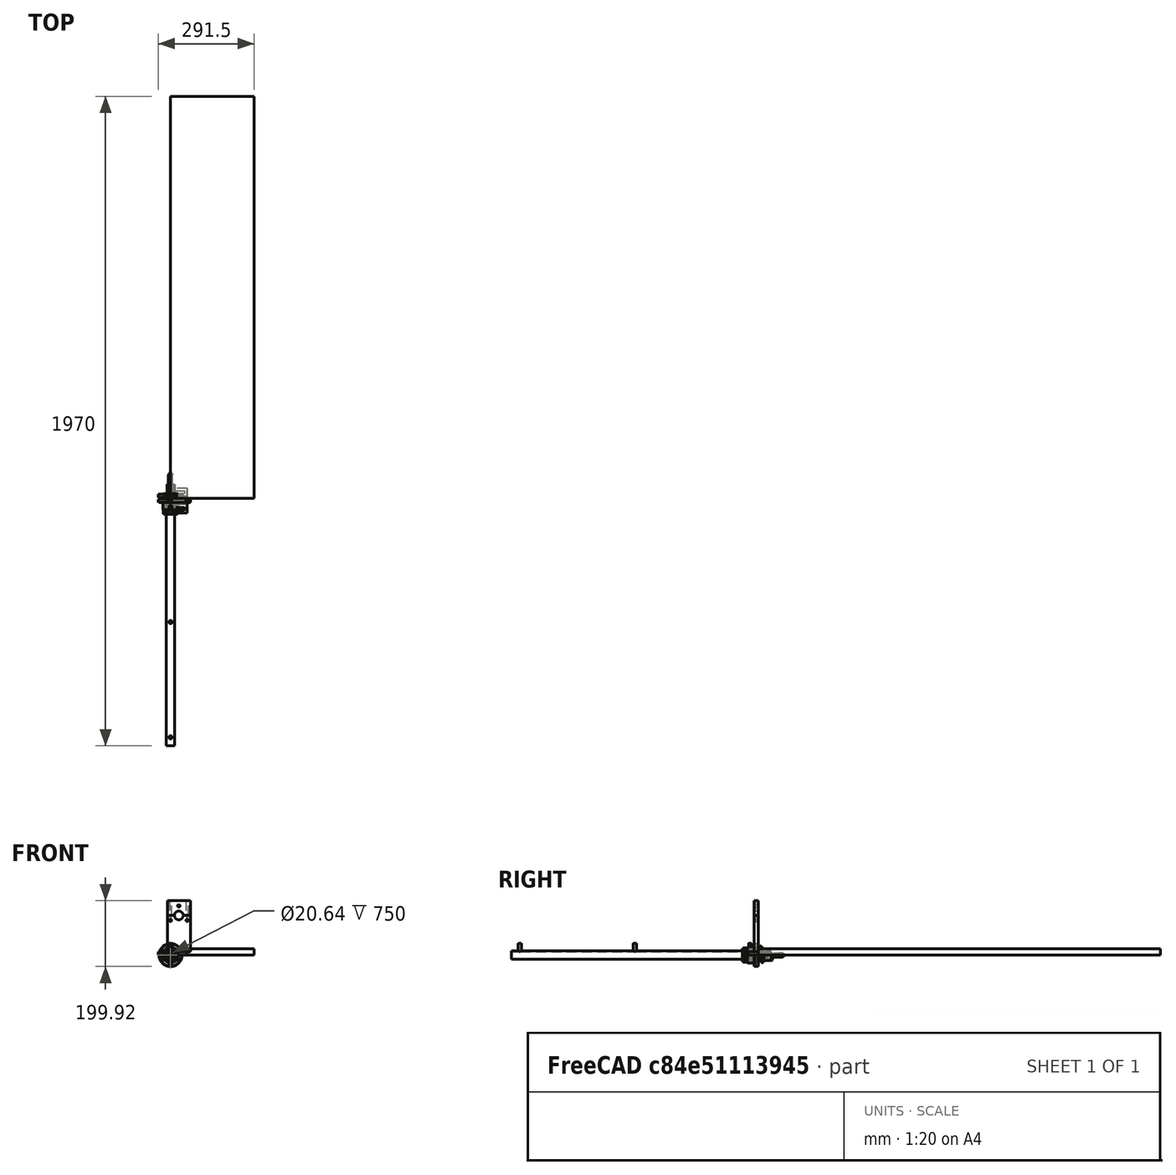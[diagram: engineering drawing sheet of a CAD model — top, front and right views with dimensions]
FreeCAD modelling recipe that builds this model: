
FCSTD DOCUMENT  (FreeCAD 0.19R24291 (Git))
Label: CEAS2a
License: All rights reserved
LicenseURL: http://en.wikipedia.org/wiki/All_rights_reserved
objects: Part::Feature×69, Part::Cut×64, Sketcher::SketchObject×60, PartDesign::Pad×60, PartDesign::Body×59, Part::Compound2×15, App::Part×14, TechDraw::DrawViewPart×8, Part::Chamfer×6, Part::MultiFuse×5, TechDraw::DrawViewDimension×4, TechDraw::DrawViewBalloon×4, TechDraw::DrawViewAnnotation×4, Part::Fillet×2, TechDraw::DrawSVGTemplate×1, TechDraw::DrawPage×1, Part::Sphere×1
note: 386 computed .brp shape members not serialized (recipe doc carries the construction recipe); baked Part::Feature solids carry a one-line shape summary decoded from their .brp

FEATURE [Sketcher::SketchObject] Sketch
  FullyConstrained = true
  MapMode = 5
  Support = -> [XY_Plane001]
  sketch-geometry (4):
    g0: LineSegment StartX=0 StartY=1220 StartZ=0 EndX=254 EndY=1220 EndZ=0
    g1: LineSegment StartX=254 StartY=1220 StartZ=0 EndX=254 EndY=0 EndZ=0
    g2: LineSegment StartX=254 StartY=0 StartZ=0 EndX=0 EndY=0 EndZ=0
    g3: LineSegment StartX=0 StartY=0 StartZ=0 EndX=0 EndY=1220 EndZ=0
  constraints (11):
    c: Coincident(g0,g1)
    c: Coincident(g1,g2)
    c: Coincident(g2,g3)
    c: Coincident(g3,g0)
    c: Horizontal(g0)
    c: Horizontal(g2)
    c: Vertical(g1)
    c: Vertical(g3)
    c: DistanceY(g3,g3) = 1220
    c: Coincident(g2,g-1)
    c: DistanceX(g2,g2) = 254
FEATURE [PartDesign::Pad] Pad
  AllowMultiFace = false
  Direction = (1,1,1)
  Length = 19.05
  Length2 = 100
  Profile = -> Sketch
  Type = 0
FEATURE [PartDesign::Body] Body  label="BasePlate001"
  Group = -> [Sketch,Pad]
  Origin = -> Origin001
  Tip = -> Pad
FEATURE [App::Part] Part  label="BasePlate"
  Group = -> [Body]
  Origin = -> Origin
FEATURE [Sketcher::SketchObject] Sketch001
  FullyConstrained = true
  MapMode = 5
  Placement = pos=(0,0,0) rot=(1,0,0;1.5708rad)
  Support = -> [XZ_Plane003]
  sketch-geometry (6):
    g0: LineSegment StartX=0 StartY=0 StartZ=0 EndX=0 EndY=110 EndZ=0
    g1: LineSegment StartX=0 StartY=110 StartZ=0 EndX=21.675 EndY=110 EndZ=0
    g2: ArcOfCircle CenterX=35 CenterY=110 CenterZ=0 NormalX=0 NormalY=0 NormalZ=1 AngleXU=0 Radius=13.325 StartAngle=3.14159 EndAngle=6.28319
    g3: LineSegment StartX=48.325 StartY=110 StartZ=0 EndX=70 EndY=110 EndZ=0
    g4: LineSegment StartX=70 StartY=110 StartZ=0 EndX=70 EndY=0 EndZ=0
    g5: LineSegment StartX=70 StartY=0 StartZ=0 EndX=0 EndY=0 EndZ=0
  constraints (18):
    c: DistanceX(g5,g5) = 70
    c: Coincident(g5,g0)
    c: Coincident(g1,g2)
    c: Coincident(g1,g0)
    c: Coincident(g2,g3)
    c: Coincident(g3,g4)
    c: Coincident(g5,g4)
    c: Diameter(g2) = 26.65
    c: Parallel(g0,g4)
    c: DistanceY(g4,g4) = 110
    c: Equal(g0,g4)
    c: Equal(g3,g1)
    c: Perpendicular(g5,g0)
    c: Perpendicular(g4,g3)
    c: Vertical(g0)
    c: Perpendicular(g0,g1)
    c: Coincident(g0,g-1)
    c: DistanceX(g1,g2) = 26.65
FEATURE [Sketcher::SketchObject] Sketch002
  FullyConstrained = true
  MapMode = 5
  Placement = pos=(0,0,0) rot=(1,0,0;1.5708rad)
  Support = -> [XZ_Plane004]
  sketch-geometry (6):
    g0: LineSegment StartX=-20 StartY=110 StartZ=0 EndX=-20 EndY=155 EndZ=0
    g1: LineSegment StartX=-20 StartY=155 StartZ=0 EndX=50 EndY=155 EndZ=0
    g2: LineSegment StartX=50 StartY=155 StartZ=0 EndX=50 EndY=110 EndZ=0
    g3: LineSegment StartX=50 StartY=110 StartZ=0 EndX=28.325 EndY=110 EndZ=0
    g4: LineSegment StartX=-20 StartY=110 StartZ=0 EndX=1.675 EndY=110 EndZ=0
    g5: ArcOfCircle CenterX=15 CenterY=110 CenterZ=0 NormalX=0 NormalY=0 NormalZ=1 AngleXU=0 Radius=13.325 StartAngle=2.48459e-06 EndAngle=3.14159
  constraints (19):
    c: Diameter(g5) = 26.65
    c: DistanceX(g1,g1) = 70
    c: Coincident(g0,g1)
    c: Coincident(g1,g2)
    c: Coincident(g2,g3)
    c: Coincident(g5,g3)
    c: Coincident(g5,g4)
    c: Coincident(g0,g4)
    c: DistanceY(g2,g2) = 45
    c: Equal(g2,g0)
    c: Horizontal(g4)
    c: Equal(g4,g3)
    c: Vertical(g0)
    c: Horizontal(g1)
    c: Perpendicular(g2,g1)
    c: Perpendicular(g2,g3)
    c: DistanceY(g-1,g0) = 110
    c: DistanceX(g-1,g2) = 50
    c: DistanceX(g4,g3) = 26.65
FEATURE [PartDesign::Pad] Pad001
  AllowMultiFace = false
  Direction = (1,1,1)
  Length = 12.7
  Length2 = 100
  Placement = pos=(0,0,0) rot=(1,0,0;1.5708rad)
  Profile = -> Sketch001
  Type = 0
FEATURE [PartDesign::Body] Body001  label="BraceLower"
  Group = -> [Sketch001,Pad001]
  Origin = -> Origin003
  Placement = pos=(-10,0,10) rot=(0,0,1;0rad)
  Tip = -> Pad001
FEATURE [PartDesign::Pad] Pad002
  AllowMultiFace = false
  Direction = (1,1,1)
  Length = 12.7
  Length2 = 100
  Placement = pos=(0,0,0) rot=(1,0,0;1.5708rad)
  Profile = -> Sketch002
  Type = 0
FEATURE [PartDesign::Body] Body002  label="Brace1Upper"
  Group = -> [Sketch002,Pad002]
  Origin = -> Origin004
  Placement = pos=(10,0,10) rot=(0,0,1;0rad)
  Tip = -> Pad002
FEATURE [Part::Feature] Solid  label="19227-E0W"
  Placement = pos=(25,-6.35,5.1905) rot=(1,0,0;1.5708rad)
  shape: bbox 50 x 75 x 10 mm, 234 faces (baked)
FEATURE [Part::Feature] Solid002  label="19225-E0W"
  Placement = pos=(0,0,5) rot=(1,0,0;1.5708rad)
  shape: bbox 75 x 24.99 x 10 mm, 221 faces (baked)
FEATURE [Part::Feature] Solid003
  shape: bbox 25 x 75 x 25 mm, 25 faces (baked)
FEATURE [Part::Feature] Solid004
  shape: bbox 15.88 x 5.969 x 15.88 mm, 19 faces (baked)
FEATURE [Part::Feature] Solid005
  shape: bbox 14.48 x 14.48 x 16.13 mm, 310 faces (baked)
FEATURE [Part::Feature] Solid006
  shape: bbox 2.997 x 2.997 x 3.556 mm, 8 faces (baked)
FEATURE [Part::Feature] Solid007
  shape: bbox 3.52 x 3.049 x 7.519 mm, 25 faces (baked)
FEATURE [Part::Feature] Solid008
  shape: bbox 3.482 x 3.482 x 3.175 mm, 21 faces (baked)
FEATURE [Part::Compound2] Compound  label="23133-E0W"
  Links = -> [Solid003,Solid004,Solid005,Solid006,Solid007,Solid008]
  Placement = pos=(-1.27,-4.75,41.95) rot=(1,0,0;1.5708rad)
FEATURE [Part::Feature] Solid009
  shape: bbox 12.67 x 75.01 x 12.67 mm, 32 faces (baked)
FEATURE [Part::Feature] Solid010
  shape: bbox 4.001 x 12 x 4.001 mm, 40 faces (baked)
FEATURE [Part::Compound2] Compound001  label="0332-E0W"
  Links = -> [Solid009,Solid010]
  Placement = pos=(0,0,22.896) rot=(1,0,0;1.5708rad)
FEATURE [Part::Feature] Solid011
  shape: bbox 30.48 x 37.34 x 10.16 mm, 236 faces (baked)
FEATURE [Part::Feature] Solid012
  shape: bbox 26.29 x 26.29 x 2.032 mm, 29 faces (baked)
FEATURE [Part::Compound2] Compound002  label="0001-E0W"
  Links = -> [Solid011,Solid012]
  Placement = pos=(0,-5.05,120) rot=(1,0,0;1.5708rad)
FEATURE [App::Part] Part003  label="Lens1"
  Group = -> [Solid002,Solid008,Solid006,Solid003,Solid005,Solid007,Solid004,Compound,Solid009,Solid010,Compound001,Solid012,Solid011,Compound002]
  Origin = -> Origin008
  Placement = pos=(127,100,19.05) rot=(0,0,1;0rad)
FEATURE [Part::Feature] Solid013  label="19225-E0W001"
  Placement = pos=(0,0,5) rot=(1,0,0;1.5708rad)
  shape: bbox 75 x 24.99 x 10 mm, 221 faces (baked)
FEATURE [Part::Feature] Solid014
  shape: bbox 25 x 75 x 25 mm, 25 faces (baked)
FEATURE [Part::Feature] Solid015
  shape: bbox 15.88 x 5.969 x 15.88 mm, 19 faces (baked)
FEATURE [Part::Feature] Solid016
  shape: bbox 14.48 x 14.48 x 16.13 mm, 310 faces (baked)
FEATURE [Part::Feature] Solid017
  shape: bbox 2.997 x 2.997 x 3.556 mm, 8 faces (baked)
FEATURE [Part::Feature] Solid018
  shape: bbox 3.52 x 3.049 x 7.519 mm, 25 faces (baked)
FEATURE [Part::Feature] Solid019
  shape: bbox 3.482 x 3.482 x 3.175 mm, 21 faces (baked)
FEATURE [Part::Compound2] Compound003  label="23133-E0W001"
  Links = -> [Solid014,Solid015,Solid016,Solid017,Solid018,Solid019]
  Placement = pos=(-1.27,-4.75,41.95) rot=(1,0,0;1.5708rad)
FEATURE [Part::Feature] Solid020
  shape: bbox 12.67 x 75.01 x 12.67 mm, 32 faces (baked)
FEATURE [Part::Feature] Solid021
  shape: bbox 4.001 x 12 x 4.001 mm, 40 faces (baked)
FEATURE [Part::Compound2] Compound004  label="0332-E0W001"
  Links = -> [Solid020,Solid021]
  Placement = pos=(0,0,22.896) rot=(1,0,0;1.5708rad)
FEATURE [Part::Feature] Solid022
  shape: bbox 30.48 x 37.34 x 10.16 mm, 236 faces (baked)
FEATURE [Part::Feature] Solid023
  shape: bbox 26.29 x 26.29 x 2.032 mm, 29 faces (baked)
FEATURE [Part::Compound2] Compound005  label="0001-E0W001"
  Links = -> [Solid022,Solid023]
  Placement = pos=(0,-5.05,120) rot=(1,0,0;1.5708rad)
FEATURE [App::Part] Part004  label="Lens2"
  Group = -> [Solid013,Solid019,Solid017,Solid014,Solid016,Solid018,Solid015,Compound003,Solid020,Solid021,Compound004,Solid023,Solid022,Compound005]
  Origin = -> Origin009
  Placement = pos=(127,200,19.05) rot=(0,0,1;0rad)
FEATURE [Part::Feature] Solid024
  shape: bbox 26.29 x 26.29 x 2.032 mm, 29 faces (baked)
FEATURE [Part::Feature] Solid025
  shape: bbox 30.48 x 37.34 x 10.16 mm, 236 faces (baked)
FEATURE [Part::Compound2] Compound006  label="0001-E0W002"
  Links = -> [Solid025,Solid024]
  Placement = pos=(0,-5.05,120) rot=(1,0,0;1.5708rad)
FEATURE [Part::Feature] Solid026
  shape: bbox 2.997 x 2.997 x 3.556 mm, 8 faces (baked)
FEATURE [Part::Feature] Solid027
  shape: bbox 14.48 x 14.48 x 16.13 mm, 310 faces (baked)
FEATURE [Part::Feature] Solid028
  shape: bbox 25 x 75 x 25 mm, 25 faces (baked)
FEATURE [Part::Feature] Solid029
  shape: bbox 15.88 x 5.969 x 15.88 mm, 19 faces (baked)
FEATURE [Part::Feature] Solid030
  shape: bbox 3.482 x 3.482 x 3.175 mm, 21 faces (baked)
FEATURE [Part::Feature] Solid031
  shape: bbox 3.52 x 3.049 x 7.519 mm, 25 faces (baked)
FEATURE [Part::Compound2] Compound007  label="23133-E0W002"
  Links = -> [Solid028,Solid029,Solid027,Solid026,Solid031,Solid030]
  Placement = pos=(-1.27,-4.75,41.95) rot=(1,0,0;1.5708rad)
FEATURE [Part::Feature] Solid032  label="19225-E0W002"
  Placement = pos=(0,0,5) rot=(1,0,0;1.5708rad)
  shape: bbox 75 x 24.99 x 10 mm, 221 faces (baked)
FEATURE [Part::Feature] Solid033
  shape: bbox 12.67 x 75.01 x 12.67 mm, 32 faces (baked)
FEATURE [Part::Feature] Solid034
  shape: bbox 4.001 x 12 x 4.001 mm, 40 faces (baked)
FEATURE [Part::Compound2] Compound008  label="0332-E0W002"
  Links = -> [Solid033,Solid034]
  Placement = pos=(0,0,22.896) rot=(1,0,0;1.5708rad)
FEATURE [App::Part] Part005  label="Lens3"
  Group = -> [Solid032,Solid030,Solid026,Solid028,Solid027,Solid031,Solid029,Compound007,Solid033,Solid034,Compound008,Solid024,Solid025,Compound006]
  Origin = -> Origin010
  Placement = pos=(127,1150,19.05) rot=(0,0,1;0rad)
FEATURE [Sketcher::SketchObject] Sketch005
  FullyConstrained = true
  MapMode = 5
  Placement = pos=(0,0,0) rot=(1,0,0;1.5708rad)
  Support = -> [XZ_Plane015]
  sketch-geometry (2):
    g0: Circle CenterX=0 CenterY=0 CenterZ=0 NormalX=0 NormalY=0 NormalZ=1 AngleXU=0 Radius=12.7
    g1: Circle CenterX=0 CenterY=0 CenterZ=0 NormalX=0 NormalY=0 NormalZ=1 AngleXU=0 Radius=10.3187
  constraints (4):
    c: Coincident(g0,g-1)
    c: Coincident(g1,g0)
    c: Diameter(g0) = 25.4
    c: Diameter(g1) = 20.6375
FEATURE [PartDesign::Pad] Pad005
  Direction = (1,1,1)
  Length = 750
  Length2 = 100
  Placement = pos=(0,0,0) rot=(1,0,0;1.5708rad)
  Profile = -> Sketch005
  Type = 0
FEATURE [PartDesign::Body] Body005
  Group = -> [Sketch005,Pad005]
  Origin = -> Origin015
  Tip = -> Pad005
FEATURE [Sketcher::SketchObject] Sketch006
  FullyConstrained = true
  MapMode = 5
  Support = -> [XY_Plane016]
  sketch-geometry (2):
    g0: Circle CenterX=0 CenterY=0 CenterZ=0 NormalX=0 NormalY=0 NormalZ=1 AngleXU=0 Radius=4.7625
    g1: Circle CenterX=0 CenterY=0 CenterZ=0 NormalX=0 NormalY=0 NormalZ=1 AngleXU=0 Radius=3.8695
  constraints (4):
    c: Coincident(g0,g-1)
    c: Coincident(g1,g0)
    c: Diameter(g0) = 9.525
    c: Diameter(g1) = 7.739
FEATURE [PartDesign::Pad] Pad006
  Direction = (1,1,1)
  Length = 25.4
  Length2 = 100
  Profile = -> Sketch006
  Type = 0
FEATURE [PartDesign::Body] Body006
  Group = -> [Sketch006,Pad006]
  Origin = -> Origin016
  Placement = pos=(0,-25.4,9.55) rot=(0,0,1;0rad)
  Tip = -> Pad006
FEATURE [Sketcher::SketchObject] Sketch007
  FullyConstrained = true
  MapMode = 5
  Support = -> [XY_Plane017]
  sketch-geometry (2):
    g0: Circle CenterX=0 CenterY=0 CenterZ=0 NormalX=0 NormalY=0 NormalZ=1 AngleXU=0 Radius=4.7625
    g1: Circle CenterX=0 CenterY=0 CenterZ=0 NormalX=0 NormalY=0 NormalZ=1 AngleXU=0 Radius=3.8695
  constraints (4):
    c: Coincident(g0,g-1)
    c: Coincident(g1,g0)
    c: Diameter(g0) = 9.525
    c: Diameter(g1) = 7.739
FEATURE [PartDesign::Pad] Pad007
  Direction = (1,1,1)
  Length = 25.4
  Length2 = 100
  Profile = -> Sketch007
  Type = 0
FEATURE [PartDesign::Body] Body007
  Group = -> [Sketch007,Pad007]
  Origin = -> Origin017
  Placement = pos=(0,-375,9.55) rot=(0,0,1;0rad)
  Tip = -> Pad007
FEATURE [Sketcher::SketchObject] Sketch008
  FullyConstrained = true
  MapMode = 5
  Support = -> [XY_Plane018]
  sketch-geometry (2):
    g0: Circle CenterX=0 CenterY=0 CenterZ=0 NormalX=0 NormalY=0 NormalZ=1 AngleXU=0 Radius=4.7625
    g1: Circle CenterX=0 CenterY=0 CenterZ=0 NormalX=0 NormalY=0 NormalZ=1 AngleXU=0 Radius=3.8695
  constraints (4):
    c: Coincident(g0,g-1)
    c: Coincident(g1,g0)
    c: Diameter(g0) = 9.525
    c: Diameter(g1) = 7.739
FEATURE [PartDesign::Pad] Pad008
  Direction = (1,1,1)
  Length = 25.4
  Length2 = 100
  Profile = -> Sketch008
  Type = 0
FEATURE [PartDesign::Body] Body008
  Group = -> [Sketch008,Pad008]
  Origin = -> Origin018
  Placement = pos=(0,-724.6,9.55) rot=(0,0,1;0rad)
  Tip = -> Pad008
FEATURE [Sketcher::SketchObject] Sketch009
  FullyConstrained = true
  MapMode = 5
  Support = -> [XY_Plane020]
  sketch-geometry (1):
    g0: Circle CenterX=0 CenterY=0 CenterZ=0 NormalX=0 NormalY=0 NormalZ=1 AngleXU=0 Radius=4.7625
  constraints (2):
    c: Coincident(g0,g-1)
    c: Diameter(g0) = 9.525
FEATURE [PartDesign::Pad] Pad009
  Direction = (1,1,1)
  Length = 25.4
  Length2 = 100
  Profile = -> Sketch009
  Type = 0
FEATURE [PartDesign::Body] Body009
  Group = -> [Sketch009,Pad009]
  Origin = -> Origin019
  Placement = pos=(0,-25.4,0) rot=(0,0,1;0rad)
  Tip = -> Pad009
FEATURE [Sketcher::SketchObject] Sketch010
  FullyConstrained = true
  MapMode = 5
  Support = -> [XY_Plane021]
  sketch-geometry (1):
    g0: Circle CenterX=0 CenterY=0 CenterZ=0 NormalX=0 NormalY=0 NormalZ=1 AngleXU=0 Radius=4.7625
  constraints (2):
    c: Coincident(g0,g-1)
    c: Diameter(g0) = 9.525
FEATURE [PartDesign::Pad] Pad010
  Direction = (1,1,1)
  Length = 25.4
  Length2 = 100
  Profile = -> Sketch010
  Type = 0
FEATURE [PartDesign::Body] Body010
  Group = -> [Sketch010,Pad010]
  Origin = -> Origin020
  Placement = pos=(0,-375,0) rot=(0,0,1;0rad)
  Tip = -> Pad010
FEATURE [Sketcher::SketchObject] Sketch011
  FullyConstrained = true
  MapMode = 5
  Support = -> [XY_Plane022]
  sketch-geometry (1):
    g0: Circle CenterX=0 CenterY=0 CenterZ=0 NormalX=0 NormalY=0 NormalZ=1 AngleXU=0 Radius=4.7625
  constraints (2):
    c: Coincident(g0,g-1)
    c: Diameter(g0) = 9.525
FEATURE [PartDesign::Pad] Pad011
  Direction = (1,1,1)
  Length = 25.4
  Length2 = 100
  Profile = -> Sketch011
  Type = 0
FEATURE [PartDesign::Body] Body011
  Group = -> [Sketch011,Pad011]
  Origin = -> Origin021
  Placement = pos=(0,-724.6,0) rot=(0,0,1;0rad)
  Tip = -> Pad011
FEATURE [Part::Cut] Cut
  Base = -> Body005
  Tool = -> Body009
FEATURE [Part::Cut] Cut001
  Base = -> Cut
  Tool = -> Body010
FEATURE [Part::Cut] Cut002
  Base = -> Cut001
  Tool = -> Body011
FEATURE [Sketcher::SketchObject] Sketch012
  FullyConstrained = true
  MapMode = 5
  Placement = pos=(0,0,0) rot=(1,0,0;1.5708rad)
  Support = -> [XZ_Plane022]
  sketch-geometry (1):
    g0: Circle CenterX=0 CenterY=0 CenterZ=0 NormalX=0 NormalY=0 NormalZ=1 AngleXU=0 Radius=10.3187
  constraints (2):
    c: Coincident(g0,g-1)
    c: Diameter(g0) = 20.6375
FEATURE [PartDesign::Pad] Pad012
  Direction = (1,1,1)
  Length = 750
  Length2 = 100
  Placement = pos=(0,0,0) rot=(1,0,0;1.5708rad)
  Profile = -> Sketch012
  Type = 0
FEATURE [PartDesign::Body] Body012
  Group = -> [Sketch012,Pad012]
  Origin = -> Origin022
  Tip = -> Pad012
FEATURE [Part::Cut] Cut003
  Base = -> Body006
  Tool = -> Body012
FEATURE [Part::Cut] Cut004
  Base = -> Body007
  Tool = -> Body012
FEATURE [Part::Cut] Cut005
  Base = -> Body008
  Tool = -> Body012
FEATURE [Part::MultiFuse] Fusion
  Shapes = -> [Cut002,Cut005,Cut004,Cut003]
FEATURE [App::Part] Part007  label="Cavity"
  Group = -> [Body005,Body006,Body007,Body008,Body009,Body010,Body011,Cut,Cut001,Cut002,Body012,Cut005,Cut004,Cut003,Fusion]
  Origin = -> Origin014
  Placement = pos=(127,310.4,139.05) rot=(0,0,1;3.14159rad)
FEATURE [Sketcher::SketchObject] Sketch013
  FullyConstrained = true
  MapMode = 5
  Placement = pos=(0,0,0) rot=(1,0,0;1.5708rad)
  Support = -> [XZ_Plane024]
  sketch-geometry (2):
    g0: Circle CenterX=0 CenterY=0 CenterZ=0 NormalX=0 NormalY=0 NormalZ=1 AngleXU=0 Radius=34.925
    g1: Circle CenterX=0 CenterY=0 CenterZ=0 NormalX=0 NormalY=0 NormalZ=1 AngleXU=0 Radius=14.2875
  constraints (4):
    c: Coincident(g0,g-1)
    c: Coincident(g1,g0)
    c: Diameter(g1) = 28.575
    c: Diameter(g0) = 69.85
FEATURE [PartDesign::Pad] Pad013
  Direction = (1,1,1)
  Length = 12.7
  Length2 = 100
  Placement = pos=(0,0,0) rot=(1,0,0;1.5708rad)
  Profile = -> Sketch013
  Type = 0
FEATURE [PartDesign::Body] Body013
  Group = -> [Sketch013,Pad013]
  Origin = -> Origin024
  Tip = -> Pad013
FEATURE [Sketcher::SketchObject] Sketch014
  FullyConstrained = true
  MapMode = 5
  Placement = pos=(0,0,0) rot=(1,0,0;1.5708rad)
  Support = -> [XZ_Plane025]
  sketch-geometry (1):
    g0: Circle CenterX=0 CenterY=29.3687 CenterZ=0 NormalX=0 NormalY=0 NormalZ=1 AngleXU=0 Radius=3.57187
  constraints (3):
    c: PointOnObject(g0,g-2)
    c: DistanceY(g-1,g0) = 29.3687
    c: Diameter(g0) = 7.14375
FEATURE [PartDesign::Pad] Pad014
  Direction = (1,1,1)
  Length = 13
  Length2 = 100
  Placement = pos=(0,0,0) rot=(1,0,0;1.5708rad)
  Profile = -> Sketch014
  Type = 0
FEATURE [PartDesign::Body] Body014
  Group = -> [Sketch014,Pad014]
  Origin = -> Origin025
  Tip = -> Pad014
FEATURE [Part::Cut] Cut006
  Base = -> Body013
  Placement = pos=(0,0,0) rot=(0,1,0;1.0472rad)
  Tool = -> Body014
FEATURE [Part::Cut] Cut007
  Base = -> Cut006
  Placement = pos=(0,0,0) rot=(0,1,0;1.0472rad)
  Tool = -> Body014
FEATURE [Part::Cut] Cut008
  Base = -> Cut007
  Placement = pos=(0,0,0) rot=(0,1,0;1.0472rad)
  Tool = -> Body014
FEATURE [Part::Cut] Cut009
  Base = -> Cut008
  Placement = pos=(0,0,0) rot=(0,1,0;1.0472rad)
  Tool = -> Body014
FEATURE [Part::Cut] Cut010
  Base = -> Cut009
  Placement = pos=(0,0,0) rot=(0,1,0;1.0472rad)
  Tool = -> Body014
FEATURE [Part::Cut] Cut011
  Base = -> Cut010
  Tool = -> Body014
FEATURE [Sketcher::SketchObject] Sketch015
  FullyConstrained = true
  MapMode = 5
  Placement = pos=(0,0,0) rot=(1,0,0;1.5708rad)
  Support = -> [XZ_Plane026]
  sketch-geometry (2):
    g0: Circle CenterX=0 CenterY=0 CenterZ=0 NormalX=0 NormalY=0 NormalZ=1 AngleXU=0 Radius=12.7
    g1: Circle CenterX=0 CenterY=0 CenterZ=0 NormalX=0 NormalY=0 NormalZ=1 AngleXU=0 Radius=14.2875
  constraints (4):
    c: Coincident(g0,g-1)
    c: Coincident(g1,g0)
    c: Diameter(g0) = 25.4
    c: Diameter(g1) = 28.575
FEATURE [PartDesign::Pad] Pad015
  Direction = (1,1,1)
  Length = 29.21
  Length2 = 100
  Placement = pos=(0,0,0) rot=(1,0,0;1.5708rad)
  Profile = -> Sketch015
  Type = 0
FEATURE [PartDesign::Body] Body015
  Group = -> [Sketch015,Pad015]
  Origin = -> Origin026
  Placement = pos=(0,-0.16,0) rot=(0,0,1;0rad)
  Tip = -> Pad015
FEATURE [Sketcher::SketchObject] Sketch016
  FullyConstrained = true
  MapMode = 5
  Placement = pos=(0,0,0) rot=(1,0,0;1.5708rad)
  Support = -> [XZ_Plane027]
  sketch-geometry (2):
    g0: Circle CenterX=0 CenterY=0 CenterZ=0 NormalX=0 NormalY=0 NormalZ=1 AngleXU=0 Radius=12.7
    g1: Circle CenterX=0 CenterY=0 CenterZ=0 NormalX=0 NormalY=0 NormalZ=1 AngleXU=0 Radius=16.6687
  constraints (4):
    c: Coincident(g0,g-1)
    c: Coincident(g1,g0)
    c: Diameter(g0) = 25.4
    c: Diameter(g1) = 33.3375
FEATURE [PartDesign::Pad] Pad016
  Direction = (1,1,1)
  Length = 12.7
  Length2 = 100
  Placement = pos=(0,0,0) rot=(1,0,0;1.5708rad)
  Profile = -> Sketch016
  Type = 0
FEATURE [PartDesign::Body] Body016
  Group = -> [Sketch016,Pad016]
  Origin = -> Origin027
  Placement = pos=(0,-29.37,0) rot=(0,0,1;0rad)
  Tip = -> Pad016
FEATURE [Part::MultiFuse] Fusion001
  Shapes = -> [Cut011,Body015,Body016]
FEATURE [Sketcher::SketchObject] Sketch017
  FullyConstrained = true
  MapMode = 5
  Placement = pos=(0,0,0) rot=(1,0,0;1.5708rad)
  Support = -> [XZ_Plane028]
  sketch-geometry (2):
    g0: Circle CenterX=0 CenterY=0 CenterZ=0 NormalX=0 NormalY=0 NormalZ=1 AngleXU=0 Radius=12.7
    g1: Circle CenterX=0 CenterY=0 CenterZ=0 NormalX=0 NormalY=0 NormalZ=1 AngleXU=0 Radius=16.6687
  constraints (4):
    c: Coincident(g0,g-1)
    c: Coincident(g1,g0)
    c: Diameter(g0) = 25.4
    c: Diameter(g1) = 33.3375
FEATURE [PartDesign::Pad] Pad017
  Direction = (1,1,1)
  Length = 3.175
  Length2 = 100
  Placement = pos=(0,0,0) rot=(1,0,0;1.5708rad)
  Profile = -> Sketch017
  Type = 0
FEATURE [PartDesign::Body] Body017
  Group = -> [Sketch017,Pad017]
  Origin = -> Origin028
  Placement = pos=(0,-42.07,0) rot=(0,0,1;0rad)
  Tip = -> Pad017
FEATURE [Sketcher::SketchObject] Sketch018
  FullyConstrained = true
  MapMode = 5
  Placement = pos=(0,0,0) rot=(1,0,0;1.5708rad)
  Support = -> [XZ_Plane029]
  sketch-geometry (2):
    g0: Circle CenterX=0 CenterY=0 CenterZ=0 NormalX=0 NormalY=0 NormalZ=1 AngleXU=0 Radius=20.2406
    g1: Circle CenterX=0 CenterY=0 CenterZ=0 NormalX=0 NormalY=0 NormalZ=1 AngleXU=0 Radius=12.7
  constraints (4):
    c: Coincident(g0,g-1)
    c: Coincident(g1,g0)
    c: Diameter(g0) = 40.4813
    c: Diameter(g1) = 25.4
FEATURE [PartDesign::Pad] Pad018
  Direction = (1,1,1)
  Length = 19.05
  Length2 = 100
  Placement = pos=(0,0,0) rot=(1,0,0;1.5708rad)
  Profile = -> Sketch018
  Type = 0
FEATURE [PartDesign::Body] Body018
  Group = -> [Sketch018,Pad018]
  Origin = -> Origin029
  Tip = -> Pad018
FEATURE [Sketcher::SketchObject] Sketch019
  FullyConstrained = true
  MapMode = 5
  Placement = pos=(0,0,0) rot=(1,0,0;1.5708rad)
  Support = -> [XZ_Plane030]
  sketch-geometry (1):
    g0: Circle CenterX=0 CenterY=0 CenterZ=0 NormalX=0 NormalY=0 NormalZ=1 AngleXU=0 Radius=16.6687
  constraints (2):
    c: Coincident(g0,g-1)
    c: Diameter(g0) = 33.3375
FEATURE [PartDesign::Pad] Pad019
  Direction = (1,1,1)
  Length = 15.875
  Length2 = 100
  Placement = pos=(0,0,0) rot=(1,0,0;1.5708rad)
  Profile = -> Sketch019
  Type = 0
FEATURE [PartDesign::Body] Body019
  Group = -> [Sketch019,Pad019]
  Origin = -> Origin030
  Tip = -> Pad019
FEATURE [Part::Cut] Cut012
  Base = -> Body018
  Placement = pos=(0,-29.37,0) rot=(0,0,1;0rad)
  Tool = -> Body019
FEATURE [App::Part] Part008  label="CFQuick1"
  Group = -> [Body014,Cut010,Body013,Cut006,Cut008,Cut009,Cut007,Cut011,Body015,Body016,Fusion001,Body017,Body018,Body019,Cut012]
  Origin = -> Origin023
  Placement = pos=(127,274.6,139.05) rot=(0,0,1;3.14159rad)
FEATURE [Sketcher::SketchObject] Sketch020
  FullyConstrained = true
  MapMode = 5
  Placement = pos=(0,0,0) rot=(1,0,0;1.5708rad)
  Support = -> [XZ_Plane031]
  sketch-geometry (1):
    g0: Circle CenterX=0 CenterY=0 CenterZ=0 NormalX=0 NormalY=0 NormalZ=1 AngleXU=0 Radius=3.57187
  constraints (2):
    c: Coincident(g0,g-1)
    c: Diameter(g0) = 7.14375
FEATURE [PartDesign::Pad] Pad020
  Direction = (1,1,1)
  Length = 30
  Length2 = 100
  Placement = pos=(0,0,0) rot=(1,0,0;1.5708rad)
  Profile = -> Sketch020
  Type = 0
FEATURE [PartDesign::Body] Body020
  Group = -> [Sketch020,Pad020]
  Origin = -> Origin031
  Placement = pos=(25,2,149.369) rot=(0,0,1;0rad)
  Tip = -> Pad020
FEATURE [Part::Cut] Cut013
  Base = -> Body002
  Placement = pos=(100,0,0) rot=(0,0,1;0rad)
  Tool = -> Body020
FEATURE [Sketcher::SketchObject] Sketch021
  FullyConstrained = true
  MapMode = 5
  Support = -> [XY_Plane033]
  sketch-geometry (1):
    g0: Circle CenterX=0 CenterY=0 CenterZ=0 NormalX=0 NormalY=0 NormalZ=1 AngleXU=0 Radius=3.57188
  constraints (2):
    c: Coincident(g0,g-1)
    c: Diameter(g0) = 7.14375
FEATURE [PartDesign::Pad] Pad021
  Direction = (1,1,1)
  Length = 55
  Length2 = 100
  Profile = -> Sketch021
  Type = 0
FEATURE [PartDesign::Body] Body021
  Group = -> [Sketch021,Pad021]
  Origin = -> Origin032
  Placement = pos=(100,-6.35,115) rot=(0,0,1;0rad)
  Tip = -> Pad021
FEATURE [Part::Cut] Cut014
  Base = -> Cut013
  Tool = -> Body021
FEATURE [Sketcher::SketchObject] Sketch022
  FullyConstrained = true
  MapMode = 5
  Support = -> [XY_Plane034]
  sketch-geometry (1):
    g0: Circle CenterX=0 CenterY=0 CenterZ=0 NormalX=0 NormalY=0 NormalZ=1 AngleXU=0 Radius=3.57187
  constraints (2):
    c: Diameter(g0) = 7.14375
    c: Coincident(g0,g-1)
FEATURE [PartDesign::Pad] Pad022
  Direction = (1,1,1)
  Length = 55
  Length2 = 100
  Profile = -> Sketch022
  Type = 0
FEATURE [PartDesign::Body] Body022
  Group = -> [Sketch022,Pad022]
  Origin = -> Origin033
  Placement = pos=(150,-6.35,115) rot=(0,0,1;0rad)
  Tip = -> Pad022
FEATURE [Part::Cut] Cut015  label="BraceUpper"
  Base = -> Cut014
  Placement = pos=(-100,0,0) rot=(0,0,1;0rad)
  Tool = -> Body022
FEATURE [Sketcher::SketchObject] Sketch023
  FullyConstrained = true
  MapMode = 5
  Placement = pos=(0,0,0) rot=(1,0,0;1.5708rad)
  Support = -> [XZ_Plane034]
  sketch-geometry (1):
    g0: Circle CenterX=0 CenterY=0 CenterZ=0 NormalX=0 NormalY=0 NormalZ=1 AngleXU=0 Radius=3.57188
  constraints (2):
    c: Coincident(g0,g-1)
    c: Diameter(g0) = 7.14375
FEATURE [PartDesign::Pad] Pad023
  Direction = (1,1,1)
  Length = 33.7
  Length2 = 100
  Placement = pos=(0,0,0) rot=(1,0,0;1.5708rad)
  Profile = -> Sketch023
  Type = 0
FEATURE [PartDesign::Body] Body023
  Group = -> [Sketch023,Pad023]
  Origin = -> Origin034
  Placement = pos=(-0.434083,5,105.316) rot=(0,0,1;0rad)
  Tip = -> Pad023
FEATURE [Part::Cut] Cut016
  Base = -> Body001
  Tool = -> Body023
FEATURE [Sketcher::SketchObject] Sketch024
  FullyConstrained = true
  MapMode = 5
  Placement = pos=(0,0,0) rot=(1,0,0;1.5708rad)
  Support = -> [XZ_Plane035]
  sketch-geometry (1):
    g0: Circle CenterX=0 CenterY=0 CenterZ=0 NormalX=0 NormalY=0 NormalZ=1 AngleXU=0 Radius=3.57187
  constraints (2):
    c: Coincident(g0,g-1)
    c: Diameter(g0) = 7.14375
FEATURE [PartDesign::Pad] Pad024
  Direction = (1,1,1)
  Length = 50
  Length2 = 100
  Placement = pos=(0,0,0) rot=(1,0,0;1.5708rad)
  Profile = -> Sketch024
  Type = 0
FEATURE [PartDesign::Body] Body024
  Group = -> [Sketch024,Pad024]
  Origin = -> Origin035
  Placement = pos=(50.4341,10,105.316) rot=(0,0,1;0rad)
  Tip = -> Pad024
FEATURE [Part::Cut] Cut017
  Base = -> Cut016
  Placement = pos=(100,0,0) rot=(0,0,1;0rad)
  Tool = -> Body024
FEATURE [Sketcher::SketchObject] Sketch025
  FullyConstrained = true
  MapMode = 5
  Support = -> [XY_Plane037]
  sketch-geometry (1):
    g0: Circle CenterX=0 CenterY=0 CenterZ=0 NormalX=0 NormalY=0 NormalZ=1 AngleXU=0 Radius=3.57187
  constraints (2):
    c: Coincident(g0,g-1)
    c: Diameter(g0) = 7.14375
FEATURE [PartDesign::Pad] Pad025
  Direction = (1,1,1)
  Length = 6
  Length2 = 100
  Profile = -> Sketch025
  Type = 0
FEATURE [PartDesign::Body] Body025
  Group = -> [Sketch025,Pad025]
  Origin = -> Origin036
  Placement = pos=(100,-6.35,115) rot=(0,0,1;0rad)
  Tip = -> Pad025
FEATURE [Sketcher::SketchObject] Sketch026
  FullyConstrained = true
  MapMode = 5
  Support = -> [XY_Plane038]
  sketch-geometry (1):
    g0: Circle CenterX=0 CenterY=0 CenterZ=0 NormalX=0 NormalY=0 NormalZ=1 AngleXU=0 Radius=3.57187
  constraints (2):
    c: Coincident(g0,g-1)
    c: Diameter(g0) = 7.14375
FEATURE [PartDesign::Pad] Pad026
  Direction = (1,1,1)
  Length = 6
  Length2 = 100
  Profile = -> Sketch026
  Type = 0
FEATURE [PartDesign::Body] Body026
  Group = -> [Sketch026,Pad026]
  Origin = -> Origin037
  Placement = pos=(150,-6.35,115) rot=(0,0,1;0rad)
  Tip = -> Pad026
FEATURE [TechDraw::DrawSVGTemplate] Template
  EditableTexts = FC-SC=0.75
  Height = 210
  Orientation = 1
  Width = 297
FEATURE [TechDraw::DrawViewPart] View  label="Frente1"
  CoarseView = false
  Direction = (0,-1,0)
  Focus = 100
  HardHidden = false
  IsoCount = 0
  IsoHidden = false
  IsoVisible = false
  LockPosition = false
  Perspective = false
  Rotation = 0
  Scale = 0.75
  ScaleType = 0
  SeamHidden = false
  SeamVisible = true
  SmoothHidden = false
  SmoothVisible = true
  Source = -> [Cut015]
  X = 56.2727
  XDirection = (1,0,0)
  Y = 165.031
FEATURE [TechDraw::DrawViewPart] View001  label="Arriba1"
  CoarseView = false
  Direction = (0,0,1)
  Focus = 100
  HardHidden = false
  IsoCount = 0
  IsoHidden = false
  IsoVisible = false
  LockPosition = false
  Perspective = false
  Rotation = 0
  Scale = 0.75
  ScaleType = 0
  SeamHidden = false
  SeamVisible = true
  SmoothHidden = false
  SmoothVisible = true
  Source = -> [Cut015]
  X = 56.2419
  XDirection = (-1,0,0)
  Y = 120.161
FEATURE [TechDraw::DrawViewPart] View002  label="Abajo1"
  CoarseView = false
  Direction = (0,0,-1)
  Focus = 100
  HardHidden = false
  IsoCount = 0
  IsoHidden = false
  IsoVisible = false
  LockPosition = false
  Perspective = false
  Rotation = 0
  Scale = 0.75
  ScaleType = 0
  SeamHidden = false
  SeamVisible = true
  SmoothHidden = false
  SmoothVisible = true
  Source = -> [Cut015]
  X = 56.2419
  XDirection = (1,0,0)
  Y = 93.0645
FEATURE [TechDraw::DrawViewPart] View003
  CoarseView = false
  Direction = (-0.577,-0.577,0.577)
  Focus = 100
  HardHidden = false
  IsoCount = 0
  IsoHidden = false
  IsoVisible = false
  LockPosition = false
  Perspective = false
  Rotation = 0
  Scale = 0.75
  ScaleType = 0
  SeamHidden = false
  SeamVisible = true
  SmoothHidden = false
  SmoothVisible = true
  Source = -> [Cut015]
  X = 56.9275
  XDirection = (0.707,-0.707,0)
  Y = 47.3157
FEATURE [TechDraw::DrawViewDimension] Dimension
  Arbitrary = false
  ArbitraryTolerances = false
  EqualTolerance = true
  FormatSpec = %.2f
  FormatSpecOverTolerance = %+.2f
  FormatSpecUnderTolerance = %+.2f
  Inverted = false
  LockPosition = false
  MeasureType = 1
  OverTolerance = 0
  References2D = -> [View]
  Rotation = 0
  Scale = 0.75
  ScaleType = 0
  TheoreticalExact = false
  Type = 2
  UnderTolerance = 0
  X = 35.4376
  Y = 0
FEATURE [TechDraw::DrawViewDimension] Dimension001
  Arbitrary = false
  ArbitraryTolerances = false
  EqualTolerance = true
  FormatSpec = %.2f
  FormatSpecOverTolerance = %+.2f
  FormatSpecUnderTolerance = %+.2f
  Inverted = false
  LockPosition = false
  MeasureType = 1
  OverTolerance = 0
  References2D = -> [View]
  Rotation = 0
  Scale = 0.75
  ScaleType = 0
  TheoreticalExact = false
  Type = 1
  UnderTolerance = 0
  X = 0.353369
  Y = 28.8896
FEATURE [Part::Cut] Cut018
  Base = -> Cut017
  Tool = -> Body025
FEATURE [Part::Cut] Cut019  label="BraceLower001"
  Base = -> Cut018
  Placement = pos=(-100,0,0) rot=(0,0,1;0rad)
  Tool = -> Body026
FEATURE [App::Part] Part001  label="Brace1"
  Group = -> [Body001,Solid,Cut014,Cut013,Body022,Body002,Body021,Body020,Cut015,Body023,Cut016,Body024,Cut017,Body025,Body026,Cut018,Cut019]
  Origin = -> Origin002
  Placement = pos=(102,300,19.05) rot=(0,0,1;0rad)
FEATURE [TechDraw::DrawViewPart] View004  label="Frente2"
  CoarseView = false
  Direction = (0,-1,0)
  Focus = 100
  HardHidden = false
  IsoCount = 0
  IsoHidden = false
  IsoVisible = false
  LockPosition = false
  Perspective = false
  Rotation = 0
  Scale = 0.75
  ScaleType = 0
  SeamHidden = false
  SeamVisible = true
  SmoothHidden = false
  SmoothVisible = true
  Source = -> [Cut019]
  X = 160.161
  XDirection = (1,0,0)
  Y = 152.705
FEATURE [TechDraw::DrawViewPart] View005  label="Arriba2"
  CoarseView = false
  Direction = (0,0,1)
  Focus = 100
  HardHidden = false
  IsoCount = 0
  IsoHidden = false
  IsoVisible = false
  LockPosition = false
  Perspective = false
  Rotation = 0
  Scale = 0.75
  ScaleType = 0
  SeamHidden = false
  SeamVisible = true
  SmoothHidden = false
  SmoothVisible = true
  Source = -> [Cut019]
  X = 159.454
  XDirection = (1,0,0)
  Y = 93.6922
FEATURE [TechDraw::DrawViewPart] View006
  CoarseView = false
  Direction = (-0.577,-0.577,0.577)
  Focus = 100
  HardHidden = false
  IsoCount = 0
  IsoHidden = false
  IsoVisible = false
  LockPosition = false
  Perspective = false
  Rotation = 0
  Scale = 0.75
  ScaleType = 0
  SeamHidden = false
  SeamVisible = true
  SmoothHidden = false
  SmoothVisible = true
  Source = -> [Cut019]
  X = 241.79
  XDirection = (0.707,-0.707,0)
  Y = 141.044
FEATURE [TechDraw::DrawViewPart] View007  label="Abajo2"
  CoarseView = false
  Direction = (0,0,-1)
  Focus = 100
  HardHidden = false
  IsoCount = 0
  IsoHidden = false
  IsoVisible = false
  LockPosition = false
  Perspective = false
  Rotation = 0
  Scale = 0.75
  ScaleType = 0
  SeamHidden = false
  SeamVisible = true
  SmoothHidden = false
  SmoothVisible = true
  Source = -> [Cut019]
  X = 159.454
  XDirection = (1,0,0)
  Y = 71.7833
FEATURE [TechDraw::DrawViewDimension] Dimension002
  Arbitrary = false
  ArbitraryTolerances = false
  EqualTolerance = true
  FormatSpec = %.2f
  FormatSpecOverTolerance = %+.2f
  FormatSpecUnderTolerance = %+.2f
  Inverted = false
  LockPosition = false
  MeasureType = 1
  OverTolerance = 0
  References2D = -> [View004]
  Rotation = 0
  Scale = 0.75
  ScaleType = 0
  TheoreticalExact = false
  Type = 2
  UnderTolerance = 0
  X = 36.4977
  Y = 1.06011
FEATURE [TechDraw::DrawViewDimension] Dimension003
  Arbitrary = false
  ArbitraryTolerances = false
  EqualTolerance = true
  FormatSpec = %.2f
  FormatSpecOverTolerance = %+.2f
  FormatSpecUnderTolerance = %+.2f
  Inverted = false
  LockPosition = false
  MeasureType = 1
  OverTolerance = 0
  References2D = -> [View004]
  Rotation = 0
  Scale = 0.75
  ScaleType = 0
  TheoreticalExact = false
  Type = 1
  UnderTolerance = 0
  X = -4.94717
  Y = -28.5287
FEATURE [TechDraw::DrawViewBalloon] Balloon
  BubbleShape = 0
  EndType = 0
  EndTypeScale = 1
  KinkLength = 5
  LockPosition = false
  OriginX = 1.38961
  OriginY = 40.8445
  Rotation = 0
  Scale = 0.75
  ScaleType = 0
  ShapeScale = 1
  SourceView = -> View004
  Text = 1 1/8"
  TextWrapLen = -1
  X = 6.38295
  Y = 5.78933
FEATURE [TechDraw::DrawViewBalloon] Balloon001
  BubbleShape = 0
  EndType = 0
  EndTypeScale = 1
  KinkLength = 5
  LockPosition = false
  OriginX = 2.32908
  OriginY = 6.97707
  Rotation = 0
  Scale = 0.75
  ScaleType = 0
  ShapeScale = 1
  SourceView = -> View
  Text = 1/4"
  TextWrapLen = -1
  X = 23.3418
  Y = -8.7606
FEATURE [TechDraw::DrawViewBalloon] Balloon002
  BubbleShape = 6
  EndType = 0
  EndTypeScale = 1
  KinkLength = 5
  LockPosition = false
  OriginX = 26.8322
  OriginY = -1.08865
  Rotation = 0
  Scale = 0.75
  ScaleType = 0
  ShapeScale = 1
  SourceView = -> View005
  Text = Tornillos 5mm
  TextWrapLen = -1
  X = 67.2974
  Y = -9.26221
FEATURE [TechDraw::DrawViewBalloon] Balloon003
  BubbleShape = 6
  EndType = 0
  EndTypeScale = 1
  KinkLength = 5
  LockPosition = false
  OriginX = 33.3037
  OriginY = -3.42201
  Rotation = 0
  Scale = 0.75
  ScaleType = 0
  ShapeScale = 1
  SourceView = -> View007
  Text = Tornillos de Base
  TextWrapLen = -1
  X = 79.0672
  Y = -3.59405
FEATURE [TechDraw::DrawViewAnnotation] Annotation
  Font = osifont
  LineSpace = 80
  LockPosition = false
  MaxWidth = -1
  Rotation = 0
  Scale = 0.75
  ScaleType = 0
  Text = Arriba
  TextSize = 5
  TextStyle = 0
  X = 19.9839
  Y = 117
FEATURE [TechDraw::DrawViewAnnotation] Annotation001
  Font = osifont
  LineSpace = 80
  LockPosition = false
  MaxWidth = -1
  Rotation = 0
  Scale = 0.75
  ScaleType = 0
  Text = Abajo
  TextSize = 5
  TextStyle = 0
  X = 18.4355
  Y = 90.2903
FEATURE [TechDraw::DrawViewAnnotation] Annotation002
  Font = osifont
  LineSpace = 80
  LockPosition = false
  MaxWidth = -1
  Rotation = 0
  Scale = 0.75
  ScaleType = 0
  Text = Arriba
  TextSize = 5
  TextStyle = 0
  X = 114.823
  Y = 91.0645
FEATURE [TechDraw::DrawViewAnnotation] Annotation003
  Font = osifont
  LineSpace = 80
  LockPosition = false
  MaxWidth = -1
  Rotation = 0
  Scale = 0.75
  ScaleType = 0
  Text = Abajo
  TextSize = 5
  TextStyle = 0
  X = 114.823
  Y = 69.3871
FEATURE [TechDraw::DrawPage] Page
  KeepUpdated = true
  NextBalloonIndex = 7
  ProjectionType = 0
  Scale = 0.75
  Template = -> Template
  Views = -> [View,View001,View002,View003,Dimension,Dimension001,View004,View005,View006,View007,Dimension002,Dimension003,Balloon,Balloon001,Balloon002,Balloon003,Annotation,Annotation001,Annotation002,Annotation003]
FEATURE [Sketcher::SketchObject] Sketch027
  FullyConstrained = true
  MapMode = 5
  Placement = pos=(0,0,0) rot=(1,0,0;1.5708rad)
  Support = -> [XZ_Plane039]
  sketch-geometry (1):
    g0: Circle CenterX=0 CenterY=0 CenterZ=0 NormalX=0 NormalY=0 NormalZ=1 AngleXU=0 Radius=3.57187
  constraints (2):
    c: Coincident(g0,g-1)
    c: Diameter(g0) = 7.14375
FEATURE [PartDesign::Pad] Pad028
  Direction = (1,1,1)
  Length = 30
  Length2 = 100
  Placement = pos=(0,0,0) rot=(1,0,0;1.5708rad)
  Profile = -> Sketch027
  Type = 0
FEATURE [PartDesign::Body] Body035
  Group = -> [Sketch027,Pad028]
  Origin = -> Origin038
  Placement = pos=(25,2,149.369) rot=(0,0,1;0rad)
  Tip = -> Pad028
FEATURE [Sketcher::SketchObject] Sketch028
  FullyConstrained = true
  MapMode = 5
  Support = -> [XY_Plane040]
  sketch-geometry (1):
    g0: Circle CenterX=0 CenterY=0 CenterZ=0 NormalX=0 NormalY=0 NormalZ=1 AngleXU=0 Radius=3.57188
  constraints (2):
    c: Coincident(g0,g-1)
    c: Diameter(g0) = 7.14375
FEATURE [PartDesign::Pad] Pad027
  Direction = (1,1,1)
  Length = 55
  Length2 = 100
  Profile = -> Sketch028
  Type = 0
FEATURE [PartDesign::Body] Body034
  Group = -> [Sketch028,Pad027]
  Origin = -> Origin039
  Placement = pos=(100,-6.35,115) rot=(0,0,1;0rad)
  Tip = -> Pad027
FEATURE [Sketcher::SketchObject] Sketch029
  FullyConstrained = true
  MapMode = 5
  Support = -> [XY_Plane041]
  sketch-geometry (1):
    g0: Circle CenterX=0 CenterY=0 CenterZ=0 NormalX=0 NormalY=0 NormalZ=1 AngleXU=0 Radius=3.57187
  constraints (2):
    c: Diameter(g0) = 7.14375
    c: Coincident(g0,g-1)
FEATURE [Sketcher::SketchObject] Sketch030
  FullyConstrained = true
  MapMode = 5
  Placement = pos=(0,0,0) rot=(1,0,0;1.5708rad)
  Support = -> [XZ_Plane046]
  sketch-geometry (1):
    g0: Circle CenterX=0 CenterY=0 CenterZ=0 NormalX=0 NormalY=0 NormalZ=1 AngleXU=0 Radius=3.57188
  constraints (2):
    c: Coincident(g0,g-1)
    c: Diameter(g0) = 7.14375
FEATURE [PartDesign::Pad] Pad030
  Direction = (1,1,1)
  Length = 33.7
  Length2 = 100
  Placement = pos=(0,0,0) rot=(1,0,0;1.5708rad)
  Profile = -> Sketch030
  Type = 0
FEATURE [PartDesign::Body] Body027
  Group = -> [Sketch030,Pad030]
  Origin = -> Origin045
  Placement = pos=(-0.434083,5,105.316) rot=(0,0,1;0rad)
  Tip = -> Pad030
FEATURE [Sketcher::SketchObject] Sketch031
  FullyConstrained = true
  MapMode = 5
  Placement = pos=(0,0,0) rot=(1,0,0;1.5708rad)
  Support = -> [XZ_Plane045]
  sketch-geometry (6):
    g0: LineSegment StartX=-20 StartY=110 StartZ=0 EndX=-20 EndY=155 EndZ=0
    g1: LineSegment StartX=-20 StartY=155 StartZ=0 EndX=50 EndY=155 EndZ=0
    g2: LineSegment StartX=50 StartY=155 StartZ=0 EndX=50 EndY=110 EndZ=0
    g3: LineSegment StartX=50 StartY=110 StartZ=0 EndX=28.325 EndY=110 EndZ=0
    g4: LineSegment StartX=-20 StartY=110 StartZ=0 EndX=1.675 EndY=110 EndZ=0
    g5: ArcOfCircle CenterX=15 CenterY=110 CenterZ=0 NormalX=0 NormalY=0 NormalZ=1 AngleXU=0 Radius=13.325 StartAngle=2.48459e-06 EndAngle=3.14159
  constraints (19):
    c: Diameter(g5) = 26.65
    c: DistanceX(g1,g1) = 70
    c: Coincident(g0,g1)
    c: Coincident(g1,g2)
    c: Coincident(g2,g3)
    c: Coincident(g5,g3)
    c: Coincident(g5,g4)
    c: Coincident(g0,g4)
    c: DistanceY(g2,g2) = 45
    c: Equal(g2,g0)
    c: Horizontal(g4)
    c: Equal(g4,g3)
    c: Vertical(g0)
    c: Horizontal(g1)
    c: Perpendicular(g2,g1)
    c: Perpendicular(g2,g3)
    c: DistanceY(g-1,g0) = 110
    c: DistanceX(g-1,g2) = 50
    c: DistanceX(g4,g3) = 26.65
FEATURE [PartDesign::Pad] Pad033
  AllowMultiFace = false
  Direction = (1,1,1)
  Length = 12.7
  Length2 = 100
  Placement = pos=(0,0,0) rot=(1,0,0;1.5708rad)
  Profile = -> Sketch031
  Type = 0
FEATURE [PartDesign::Body] Body033  label="Brace1Upper001"
  Group = -> [Sketch031,Pad033]
  Origin = -> Origin042
  Placement = pos=(10,0,10) rot=(0,0,1;0rad)
  Tip = -> Pad033
FEATURE [Part::Cut] Cut021
  Base = -> Body033
  Placement = pos=(100,0,0) rot=(0,0,1;0rad)
  Tool = -> Body035
FEATURE [Part::Cut] Cut020
  Base = -> Cut021
  Tool = -> Body034
FEATURE [Sketcher::SketchObject] Sketch032
  FullyConstrained = true
  MapMode = 5
  Placement = pos=(0,0,0) rot=(1,0,0;1.5708rad)
  Support = -> [XZ_Plane044]
  sketch-geometry (6):
    g0: LineSegment StartX=0 StartY=0 StartZ=0 EndX=0 EndY=110 EndZ=0
    g1: LineSegment StartX=0 StartY=110 StartZ=0 EndX=21.675 EndY=110 EndZ=0
    g2: ArcOfCircle CenterX=35 CenterY=110 CenterZ=0 NormalX=0 NormalY=0 NormalZ=1 AngleXU=0 Radius=13.325 StartAngle=3.14159 EndAngle=6.28319
    g3: LineSegment StartX=48.325 StartY=110 StartZ=0 EndX=70 EndY=110 EndZ=0
    g4: LineSegment StartX=70 StartY=110 StartZ=0 EndX=70 EndY=0 EndZ=0
    g5: LineSegment StartX=70 StartY=0 StartZ=0 EndX=0 EndY=0 EndZ=0
  constraints (18):
    c: DistanceX(g5,g5) = 70
    c: Coincident(g5,g0)
    c: Coincident(g1,g2)
    c: Coincident(g1,g0)
    c: Coincident(g2,g3)
    c: Coincident(g3,g4)
    c: Coincident(g5,g4)
    c: Diameter(g2) = 26.65
    c: Parallel(g0,g4)
    c: DistanceY(g4,g4) = 110
    c: Equal(g0,g4)
    c: Equal(g3,g1)
    c: Perpendicular(g5,g0)
    c: Perpendicular(g4,g3)
    c: Vertical(g0)
    c: Perpendicular(g0,g1)
    c: Coincident(g0,g-1)
    c: DistanceX(g1,g2) = 26.65
FEATURE [PartDesign::Pad] Pad034
  AllowMultiFace = false
  Direction = (1,1,1)
  Length = 12.7
  Length2 = 100
  Placement = pos=(0,0,0) rot=(1,0,0;1.5708rad)
  Profile = -> Sketch032
  Type = 0
FEATURE [PartDesign::Body] Body032  label="BraceLower002"
  Group = -> [Sketch032,Pad034]
  Origin = -> Origin041
  Placement = pos=(-10,0,10) rot=(0,0,1;0rad)
  Tip = -> Pad034
FEATURE [Sketcher::SketchObject] Sketch033
  FullyConstrained = true
  MapMode = 5
  Placement = pos=(0,0,0) rot=(1,0,0;1.5708rad)
  Support = -> [XZ_Plane047]
  sketch-geometry (1):
    g0: Circle CenterX=0 CenterY=0 CenterZ=0 NormalX=0 NormalY=0 NormalZ=1 AngleXU=0 Radius=3.57187
  constraints (2):
    c: Coincident(g0,g-1)
    c: Diameter(g0) = 7.14375
FEATURE [PartDesign::Pad] Pad032
  Direction = (1,1,1)
  Length = 50
  Length2 = 100
  Placement = pos=(0,0,0) rot=(1,0,0;1.5708rad)
  Profile = -> Sketch033
  Type = 0
FEATURE [PartDesign::Body] Body028
  Group = -> [Sketch033,Pad032]
  Origin = -> Origin046
  Placement = pos=(50.4341,10,105.316) rot=(0,0,1;0rad)
  Tip = -> Pad032
FEATURE [Part::Cut] Cut022
  Base = -> Body032
  Tool = -> Body027
FEATURE [Part::Cut] Cut025
  Base = -> Cut022
  Placement = pos=(100,0,0) rot=(0,0,1;0rad)
  Tool = -> Body028
FEATURE [PartDesign::Pad] Pad035
  Direction = (1,1,1)
  Length = 55
  Length2 = 100
  Profile = -> Sketch029
  Type = 0
FEATURE [PartDesign::Body] Body029
  Group = -> [Sketch029,Pad035]
  Origin = -> Origin043
  Placement = pos=(150,-6.35,115) rot=(0,0,1;0rad)
  Tip = -> Pad035
FEATURE [Part::Cut] Cut024  label="BraceUpper001"
  Base = -> Cut020
  Placement = pos=(-100,0,0) rot=(0,0,1;0rad)
  Tool = -> Body029
FEATURE [Part::Feature] Solid035  label="19227-E0W001"
  Placement = pos=(25,-6.35,5.1905) rot=(1,0,0;1.5708rad)
  shape: bbox 50 x 75 x 10 mm, 234 faces (baked)
FEATURE [Sketcher::SketchObject] Sketch034
  FullyConstrained = true
  MapMode = 5
  Support = -> [XY_Plane042]
  sketch-geometry (1):
    g0: Circle CenterX=0 CenterY=0 CenterZ=0 NormalX=0 NormalY=0 NormalZ=1 AngleXU=0 Radius=3.57187
  constraints (2):
    c: Coincident(g0,g-1)
    c: Diameter(g0) = 7.14375
FEATURE [PartDesign::Pad] Pad029
  Direction = (1,1,1)
  Length = 6
  Length2 = 100
  Profile = -> Sketch034
  Type = 0
FEATURE [PartDesign::Body] Body030
  Group = -> [Sketch034,Pad029]
  Origin = -> Origin047
  Placement = pos=(100,-6.35,115) rot=(0,0,1;0rad)
  Tip = -> Pad029
FEATURE [Part::Cut] Cut026
  Base = -> Cut025
  Tool = -> Body030
FEATURE [Sketcher::SketchObject] Sketch035
  FullyConstrained = true
  MapMode = 5
  Support = -> [XY_Plane043]
  sketch-geometry (1):
    g0: Circle CenterX=0 CenterY=0 CenterZ=0 NormalX=0 NormalY=0 NormalZ=1 AngleXU=0 Radius=3.57187
  constraints (2):
    c: Coincident(g0,g-1)
    c: Diameter(g0) = 7.14375
FEATURE [PartDesign::Pad] Pad031
  Direction = (1,1,1)
  Length = 6
  Length2 = 100
  Profile = -> Sketch035
  Type = 0
FEATURE [PartDesign::Body] Body031
  Group = -> [Sketch035,Pad031]
  Origin = -> Origin044
  Placement = pos=(150,-6.35,115) rot=(0,0,1;0rad)
  Tip = -> Pad031
FEATURE [Part::Cut] Cut023  label="BraceLower003"
  Base = -> Cut026
  Placement = pos=(-100,0,0) rot=(0,0,1;0rad)
  Tool = -> Body031
FEATURE [App::Part] Part009  label="Brace2"
  Group = -> [Body032,Solid035,Cut020,Cut021,Body029,Body033,Body034,Body035,Cut024,Body027,Cut022,Body028,Cut025,Body030,Body031,Cut026,Cut023]
  Origin = -> Origin040
  Placement = pos=(102,1083.74,19.05) rot=(0,0,1;0rad)
FEATURE [Sketcher::SketchObject] Sketch036
  FullyConstrained = true
  MapMode = 5
  Placement = pos=(0,0,0) rot=(1,0,0;1.5708rad)
  Support = -> [XZ_Plane055]
  sketch-geometry (2):
    g0: Circle CenterX=0 CenterY=0 CenterZ=0 NormalX=0 NormalY=0 NormalZ=1 AngleXU=0 Radius=20.2406
    g1: Circle CenterX=0 CenterY=0 CenterZ=0 NormalX=0 NormalY=0 NormalZ=1 AngleXU=0 Radius=12.7
  constraints (4):
    c: Coincident(g0,g-1)
    c: Coincident(g1,g0)
    c: Diameter(g0) = 40.4813
    c: Diameter(g1) = 25.4
FEATURE [Sketcher::SketchObject] Sketch037
  FullyConstrained = true
  MapMode = 5
  Placement = pos=(0,0,0) rot=(1,0,0;1.5708rad)
  Support = -> [XZ_Plane052]
  sketch-geometry (2):
    g0: Circle CenterX=0 CenterY=0 CenterZ=0 NormalX=0 NormalY=0 NormalZ=1 AngleXU=0 Radius=12.7
    g1: Circle CenterX=0 CenterY=0 CenterZ=0 NormalX=0 NormalY=0 NormalZ=1 AngleXU=0 Radius=16.6687
  constraints (4):
    c: Coincident(g0,g-1)
    c: Coincident(g1,g0)
    c: Diameter(g0) = 25.4
    c: Diameter(g1) = 33.3375
FEATURE [Sketcher::SketchObject] Sketch038
  FullyConstrained = true
  MapMode = 5
  Placement = pos=(0,0,0) rot=(1,0,0;1.5708rad)
  Support = -> [XZ_Plane053]
  sketch-geometry (2):
    g0: Circle CenterX=0 CenterY=0 CenterZ=0 NormalX=0 NormalY=0 NormalZ=1 AngleXU=0 Radius=12.7
    g1: Circle CenterX=0 CenterY=0 CenterZ=0 NormalX=0 NormalY=0 NormalZ=1 AngleXU=0 Radius=16.6687
  constraints (4):
    c: Coincident(g0,g-1)
    c: Coincident(g1,g0)
    c: Diameter(g0) = 25.4
    c: Diameter(g1) = 33.3375
FEATURE [PartDesign::Pad] Pad039
  Direction = (1,1,1)
  Length = 3.175
  Length2 = 100
  Placement = pos=(0,0,0) rot=(1,0,0;1.5708rad)
  Profile = -> Sketch038
  Type = 0
FEATURE [PartDesign::Pad] Pad041
  Direction = (1,1,1)
  Length = 12.7
  Length2 = 100
  Placement = pos=(0,0,0) rot=(1,0,0;1.5708rad)
  Profile = -> Sketch037
  Type = 0
FEATURE [PartDesign::Pad] Pad042
  Direction = (1,1,1)
  Length = 19.05
  Length2 = 100
  Placement = pos=(0,0,0) rot=(1,0,0;1.5708rad)
  Profile = -> Sketch036
  Type = 0
FEATURE [Sketcher::SketchObject] Sketch039
  FullyConstrained = true
  MapMode = 5
  Placement = pos=(0,0,0) rot=(1,0,0;1.5708rad)
  Support = -> [XZ_Plane051]
  sketch-geometry (2):
    g0: Circle CenterX=0 CenterY=0 CenterZ=0 NormalX=0 NormalY=0 NormalZ=1 AngleXU=0 Radius=12.7
    g1: Circle CenterX=0 CenterY=0 CenterZ=0 NormalX=0 NormalY=0 NormalZ=1 AngleXU=0 Radius=14.2875
  constraints (4):
    c: Coincident(g0,g-1)
    c: Coincident(g1,g0)
    c: Diameter(g0) = 25.4
    c: Diameter(g1) = 28.575
FEATURE [PartDesign::Pad] Pad036
  Direction = (1,1,1)
  Length = 29.21
  Length2 = 100
  Placement = pos=(0,0,0) rot=(1,0,0;1.5708rad)
  Profile = -> Sketch039
  Type = 0
FEATURE [Sketcher::SketchObject] Sketch040
  FullyConstrained = true
  MapMode = 5
  Placement = pos=(0,0,0) rot=(1,0,0;1.5708rad)
  Support = -> [XZ_Plane049]
  sketch-geometry (2):
    g0: Circle CenterX=0 CenterY=0 CenterZ=0 NormalX=0 NormalY=0 NormalZ=1 AngleXU=0 Radius=34.925
    g1: Circle CenterX=0 CenterY=0 CenterZ=0 NormalX=0 NormalY=0 NormalZ=1 AngleXU=0 Radius=14.2875
  constraints (4):
    c: Coincident(g0,g-1)
    c: Coincident(g1,g0)
    c: Diameter(g1) = 28.575
    c: Diameter(g0) = 69.85
FEATURE [PartDesign::Pad] Pad037
  Direction = (1,1,1)
  Length = 12.7
  Length2 = 100
  Placement = pos=(0,0,0) rot=(1,0,0;1.5708rad)
  Profile = -> Sketch040
  Type = 0
FEATURE [Sketcher::SketchObject] Sketch041
  FullyConstrained = true
  MapMode = 5
  Placement = pos=(0,0,0) rot=(1,0,0;1.5708rad)
  Support = -> [XZ_Plane050]
  sketch-geometry (1):
    g0: Circle CenterX=0 CenterY=29.3687 CenterZ=0 NormalX=0 NormalY=0 NormalZ=1 AngleXU=0 Radius=3.57187
  constraints (3):
    c: PointOnObject(g0,g-2)
    c: DistanceY(g-1,g0) = 29.3687
    c: Diameter(g0) = 7.14375
FEATURE [PartDesign::Pad] Pad038
  Direction = (1,1,1)
  Length = 13
  Length2 = 100
  Placement = pos=(0,0,0) rot=(1,0,0;1.5708rad)
  Profile = -> Sketch041
  Type = 0
FEATURE [PartDesign::Body] Body036
  Group = -> [Sketch039,Pad036]
  Origin = -> Origin054
  Placement = pos=(0,-0.16,0) rot=(0,0,1;0rad)
  Tip = -> Pad036
FEATURE [PartDesign::Body] Body037
  Group = -> [Sketch037,Pad041]
  Origin = -> Origin055
  Placement = pos=(0,-29.37,0) rot=(0,0,1;0rad)
  Tip = -> Pad041
FEATURE [PartDesign::Body] Body038
  Group = -> [Sketch036,Pad042]
  Origin = -> Origin050
  Tip = -> Pad042
FEATURE [PartDesign::Body] Body039
  Group = -> [Sketch040,Pad037]
  Origin = -> Origin052
  Tip = -> Pad037
FEATURE [PartDesign::Body] Body040
  Group = -> [Sketch041,Pad038]
  Origin = -> Origin053
  Tip = -> Pad038
FEATURE [Part::Cut] Cut028
  Base = -> Body039
  Placement = pos=(0,0,0) rot=(0,1,0;1.0472rad)
  Tool = -> Body040
FEATURE [Part::Cut] Cut027
  Base = -> Cut028
  Placement = pos=(0,0,0) rot=(0,1,0;1.0472rad)
  Tool = -> Body040
FEATURE [Part::Cut] Cut031
  Base = -> Cut027
  Placement = pos=(0,0,0) rot=(0,1,0;1.0472rad)
  Tool = -> Body040
FEATURE [Part::Cut] Cut032
  Base = -> Cut031
  Placement = pos=(0,0,0) rot=(0,1,0;1.0472rad)
  Tool = -> Body040
FEATURE [Part::Cut] Cut029
  Base = -> Cut032
  Placement = pos=(0,0,0) rot=(0,1,0;1.0472rad)
  Tool = -> Body040
FEATURE [Part::Cut] Cut030
  Base = -> Cut029
  Tool = -> Body040
FEATURE [Part::MultiFuse] Fusion002
  Shapes = -> [Cut030,Body036,Body037]
FEATURE [PartDesign::Body] Body041
  Group = -> [Sketch038,Pad039]
  Origin = -> Origin049
  Placement = pos=(0,-42.07,0) rot=(0,0,1;0rad)
  Tip = -> Pad039
FEATURE [Sketcher::SketchObject] Sketch042
  FullyConstrained = true
  MapMode = 5
  Placement = pos=(0,0,0) rot=(1,0,0;1.5708rad)
  Support = -> [XZ_Plane054]
  sketch-geometry (1):
    g0: Circle CenterX=0 CenterY=0 CenterZ=0 NormalX=0 NormalY=0 NormalZ=1 AngleXU=0 Radius=16.6687
  constraints (2):
    c: Coincident(g0,g-1)
    c: Diameter(g0) = 33.3375
FEATURE [PartDesign::Pad] Pad040
  Direction = (1,1,1)
  Length = 15.875
  Length2 = 100
  Placement = pos=(0,0,0) rot=(1,0,0;1.5708rad)
  Profile = -> Sketch042
  Type = 0
FEATURE [PartDesign::Body] Body042
  Group = -> [Sketch042,Pad040]
  Origin = -> Origin048
  Tip = -> Pad040
FEATURE [Part::Cut] Cut033
  Base = -> Body038
  Placement = pos=(0,-29.37,0) rot=(0,0,1;0rad)
  Tool = -> Body042
FEATURE [App::Part] Part010  label="CFQuick2"
  Group = -> [Body040,Cut029,Body039,Cut028,Cut031,Cut032,Cut027,Cut030,Body036,Body037,Fusion002,Body041,Body038,Body042,Cut033]
  Origin = -> Origin051
  Placement = pos=(127,1096.44,139.05) rot=(0,0,1;0rad)
FEATURE [Part::Feature] Solid038
  shape: bbox 25 x 75 x 25 mm, 25 faces (baked)
FEATURE [Part::Feature] Solid039  label="19225-E0W003"
  Placement = pos=(0,0,5) rot=(1,0,0;1.5708rad)
  shape: bbox 75 x 24.99 x 10 mm, 221 faces (baked)
FEATURE [Part::Feature] Solid040
  shape: bbox 2.997 x 2.997 x 3.556 mm, 8 faces (baked)
FEATURE [Part::Feature] Solid041
  shape: bbox 15.88 x 5.969 x 15.88 mm, 19 faces (baked)
FEATURE [Part::Feature] Solid042
  shape: bbox 14.48 x 14.48 x 16.13 mm, 310 faces (baked)
FEATURE [Part::Feature] Solid043
  shape: bbox 12.67 x 75.01 x 12.67 mm, 32 faces (baked)
FEATURE [Part::Feature] Solid044
  shape: bbox 4.001 x 12 x 4.001 mm, 40 faces (baked)
FEATURE [Part::Compound2] Compound010  label="0332-E0W003"
  Links = -> [Solid043,Solid044]
  Placement = pos=(0,0,18.9) rot=(1,0,0;1.5708rad)
FEATURE [Part::Feature] Solid045
  shape: bbox 3.482 x 3.482 x 3.175 mm, 21 faces (baked)
FEATURE [Part::Feature] Solid046
  shape: bbox 3.52 x 3.049 x 7.519 mm, 25 faces (baked)
FEATURE [Part::Compound2] Compound011  label="23133-E0W003"
  Links = -> [Solid038,Solid041,Solid042,Solid040,Solid046,Solid045]
  Placement = pos=(-1.27,-4.75,41.95) rot=(1,0,0;1.5708rad)
FEATURE [Part::Feature] Solid047
  shape: bbox 42.16 x 42.16 x 12.19 mm, 57 faces (baked)
FEATURE [Part::Feature] Solid048
  shape: bbox 40.64 x 40.64 x 3.304 mm, 146 faces (baked)
FEATURE [Part::Feature] Solid049
  shape: bbox 10.67 x 8.128 x 10.67 mm, 27 faces (baked)
FEATURE [Part::Feature] Solid050
  shape: bbox 8.891 x 7.113 x 7.113 mm, 34 faces (baked)
FEATURE [Part::Feature] Solid051
  shape: bbox 7.113 x 8.891 x 7.113 mm, 34 faces (baked)
FEATURE [Part::Feature] Solid052
  shape: bbox 12.97 x 12.92 x 4.572 mm, 6 faces (baked)
FEATURE [Part::Feature] Solid053
  shape: bbox 33.02 x 33.02 x 11.43 mm, 22 faces (baked)
FEATURE [Part::Feature] Solid054
  shape: bbox 35 x 35 x 3.429 mm, 18 faces (baked)
FEATURE [Part::Feature] Solid055
  shape: bbox 7.332 x 5.588 x 6.35 mm, 28 faces (baked)
FEATURE [Part::Feature] Solid056
  shape: bbox 5.588 x 6.511 x 7.325 mm, 28 faces (baked)
FEATURE [Part::Feature] Solid057
  shape: bbox 4.235 x 11.94 x 4.237 mm, 7 faces (baked)
FEATURE [Part::Feature] Solid058
  shape: bbox 11.94 x 4.155 x 4.16 mm, 7 faces (baked)
FEATURE [Part::Feature] Solid059
  shape: bbox 26.29 x 26.29 x 2.032 mm, 29 faces (baked)
FEATURE [Part::Compound2] Compound012  label="3055-E0W"
  Links = -> [Solid047,Solid048,Solid049,Solid050,Solid051,Solid052,Solid053,Solid054,Solid055,Solid056,Solid057,Solid058,Solid059]
  Placement = pos=(-1.5,-0.4,121.5) rot=(1,0,0;1.5708rad)
FEATURE [Sketcher::SketchObject] Sketch043
  FullyConstrained = true
  MapMode = 5
  Placement = pos=(0,0,0) rot=(1,0,0;1.5708rad)
  Support = -> [XZ_Plane057]
  sketch-geometry (2):
    g0: Circle CenterX=0 CenterY=0 CenterZ=0 NormalX=0 NormalY=0 NormalZ=1 AngleXU=0 Radius=34.925
    g1: Circle CenterX=0 CenterY=0 CenterZ=0 NormalX=0 NormalY=0 NormalZ=1 AngleXU=0 Radius=9.525
  constraints (4):
    c: Coincident(g0,g-1)
    c: Coincident(g1,g0)
    c: Diameter(g1) = 19.05
    c: Diameter(g0) = 69.85
FEATURE [PartDesign::Pad] Pad043
  Direction = (1,1,1)
  Length = 12.7
  Length2 = 100
  Placement = pos=(0,0,0) rot=(1,0,0;1.5708rad)
  Profile = -> Sketch043
  Type = 0
FEATURE [PartDesign::Body] Body043
  Group = -> [Sketch043,Pad043]
  Origin = -> Origin057
  Tip = -> Pad043
FEATURE [Sketcher::SketchObject] Sketch044
  FullyConstrained = true
  MapMode = 5
  Placement = pos=(0,0,0) rot=(1,0,0;1.5708rad)
  Support = -> [XZ_Plane058]
  sketch-geometry (1):
    g0: Circle CenterX=0 CenterY=29.3687 CenterZ=0 NormalX=0 NormalY=0 NormalZ=1 AngleXU=0 Radius=3.57187
  constraints (3):
    c: PointOnObject(g0,g-2)
    c: DistanceY(g-1,g0) = 29.3687
    c: Diameter(g0) = 7.14375
FEATURE [PartDesign::Pad] Pad044
  Direction = (1,1,1)
  Length = 13
  Length2 = 100
  Placement = pos=(0,0,0) rot=(1,0,0;1.5708rad)
  Profile = -> Sketch044
  Type = 0
FEATURE [PartDesign::Body] Body044
  Group = -> [Sketch044,Pad044]
  Origin = -> Origin058
  Tip = -> Pad044
FEATURE [Part::Cut] Cut034
  Base = -> Body043
  Placement = pos=(0,0,0) rot=(0,1,0;1.0472rad)
  Tool = -> Body044
FEATURE [Part::Cut] Cut035
  Base = -> Cut034
  Placement = pos=(0,0,0) rot=(0,1,0;1.0472rad)
  Tool = -> Body044
FEATURE [Part::Cut] Cut036
  Base = -> Cut035
  Placement = pos=(0,0,0) rot=(0,1,0;1.0472rad)
  Tool = -> Body044
FEATURE [Part::Cut] Cut037
  Base = -> Cut036
  Placement = pos=(0,0,0) rot=(0,1,0;1.0472rad)
  Tool = -> Body044
FEATURE [Part::Cut] Cut038
  Base = -> Cut037
  Placement = pos=(0,0,0) rot=(0,1,0;1.0472rad)
  Tool = -> Body044
FEATURE [Part::Cut] Cut039
  Base = -> Cut038
  Tool = -> Body044
FEATURE [Part::Chamfer] Chamfer
  Base = -> Cut039
  Edges = 1 edges r=1.59: [Edge3]
FEATURE [Sketcher::SketchObject] Sketch045
  FullyConstrained = true
  MapMode = 5
  Placement = pos=(0,0,0) rot=(1,0,0;1.5708rad)
  Support = -> [XZ_Plane060]
  sketch-geometry (2):
    g0: Circle CenterX=0 CenterY=0 CenterZ=0 NormalX=0 NormalY=0 NormalZ=1 AngleXU=0 Radius=6.35
    g1: Circle CenterX=0 CenterY=0 CenterZ=0 NormalX=0 NormalY=0 NormalZ=1 AngleXU=0 Radius=23.8125
  constraints (4):
    c: Coincident(g0,g-1)
    c: Coincident(g1,g0)
    c: Diameter(g1) = 47.625
    c: Diameter(g0) = 12.7
FEATURE [PartDesign::Pad] Pad045
  Direction = (1,1,1)
  Length = 25.4
  Length2 = 100
  Placement = pos=(0,0,0) rot=(1,0,0;1.5708rad)
  Profile = -> Sketch045
  Type = 0
FEATURE [PartDesign::Body] Body045
  Group = -> [Sketch045,Pad045]
  Origin = -> Origin060
  Tip = -> Pad045
FEATURE [Part::Chamfer] Chamfer001
  Base = -> Chamfer
  Edges = 1 edges r=0.79: [Edge3]
FEATURE [Sketcher::SketchObject] Sketch046
  FullyConstrained = true
  MapMode = 5
  Placement = pos=(0,0,0) rot=(1,0,0;1.5708rad)
  Support = -> [XZ_Plane061]
  sketch-geometry (1):
    g0: Circle CenterX=0 CenterY=0 CenterZ=0 NormalX=0 NormalY=0 NormalZ=1 AngleXU=0 Radius=14.2875
  constraints (2):
    c: Coincident(g0,g-1)
    c: Diameter(g0) = 28.575
FEATURE [PartDesign::Pad] Pad046
  Direction = (1,1,1)
  Length = 12.7
  Length2 = 100
  Placement = pos=(0,0,0) rot=(1,0,0;1.5708rad)
  Profile = -> Sketch046
  Type = 0
FEATURE [PartDesign::Body] Body046
  Group = -> [Sketch046,Pad046]
  Origin = -> Origin061
  Tip = -> Pad046
FEATURE [Part::Cut] Cut040
  Base = -> Body045
  Tool = -> Body046
FEATURE [Part::Chamfer] Chamfer002
  Base = -> Cut040
  Edges = 1 edges: [Edge3 r1=4.76 r2=11.11]
  Placement = pos=(0,-12.7,0) rot=(0,0,1;0rad)
FEATURE [App::Part] Part012  label="CRDmount(simple)1"
  Group = -> [Body043,Body044,Cut034,Cut035,Cut036,Cut037,Cut038,Cut039,Chamfer,Body045,Chamfer001,Body046,Cut040,Chamfer002]
  Origin = -> Origin059
  Placement = pos=(127,274.6,139.05) rot=(0,0,1;0rad)
FEATURE [Sketcher::SketchObject] Sketch047
  FullyConstrained = true
  MapMode = 5
  Placement = pos=(0,0,0) rot=(1,0,0;1.5708rad)
  Support = -> [XZ_Plane062]
  sketch-geometry (2):
    g0: Circle CenterX=0 CenterY=0 CenterZ=0 NormalX=0 NormalY=0 NormalZ=1 AngleXU=0 Radius=34.925
    g1: Circle CenterX=0 CenterY=0 CenterZ=0 NormalX=0 NormalY=0 NormalZ=1 AngleXU=0 Radius=9.525
  constraints (4):
    c: Coincident(g0,g-1)
    c: Coincident(g1,g0)
    c: Diameter(g1) = 19.05
    c: Diameter(g0) = 69.85
FEATURE [PartDesign::Pad] Pad047
  Direction = (1,1,1)
  Length = 12.7
  Length2 = 100
  Placement = pos=(0,0,0) rot=(1,0,0;1.5708rad)
  Profile = -> Sketch047
  Type = 0
FEATURE [PartDesign::Body] Body047
  Group = -> [Sketch047,Pad047]
  Origin = -> Origin063
  Tip = -> Pad047
FEATURE [Sketcher::SketchObject] Sketch048
  FullyConstrained = true
  MapMode = 5
  Placement = pos=(0,0,0) rot=(1,0,0;1.5708rad)
  Support = -> [XZ_Plane063]
  sketch-geometry (1):
    g0: Circle CenterX=0 CenterY=29.3687 CenterZ=0 NormalX=0 NormalY=0 NormalZ=1 AngleXU=0 Radius=3.57187
  constraints (3):
    c: PointOnObject(g0,g-2)
    c: DistanceY(g-1,g0) = 29.3687
    c: Diameter(g0) = 7.14375
FEATURE [PartDesign::Pad] Pad048
  Direction = (1,1,1)
  Length = 13
  Length2 = 100
  Placement = pos=(0,0,0) rot=(1,0,0;1.5708rad)
  Profile = -> Sketch048
  Type = 0
FEATURE [PartDesign::Body] Body049
  Group = -> [Sketch048,Pad048]
  Origin = -> Origin062
  Tip = -> Pad048
FEATURE [Part::Cut] Cut041
  Base = -> Body047
  Placement = pos=(0,0,0) rot=(0,1,0;1.0472rad)
  Tool = -> Body049
FEATURE [Part::Cut] Cut042
  Base = -> Cut041
  Placement = pos=(0,0,0) rot=(0,1,0;1.0472rad)
  Tool = -> Body049
FEATURE [Part::Cut] Cut043
  Base = -> Cut042
  Placement = pos=(0,0,0) rot=(0,1,0;1.0472rad)
  Tool = -> Body049
FEATURE [Part::Cut] Cut044
  Base = -> Cut043
  Placement = pos=(0,0,0) rot=(0,1,0;1.0472rad)
  Tool = -> Body049
FEATURE [Part::Cut] Cut045
  Base = -> Cut044
  Placement = pos=(0,0,0) rot=(0,1,0;1.0472rad)
  Tool = -> Body049
FEATURE [Part::Cut] Cut046
  Base = -> Cut045
  Tool = -> Body049
FEATURE [Part::Chamfer] Chamfer005
  Base = -> Cut046
  Edges = 1 edges r=1.59: [Edge3]
FEATURE [Part::Chamfer] Chamfer004
  Base = -> Chamfer005
  Edges = 1 edges r=0.79: [Edge3]
FEATURE [Sketcher::SketchObject] Sketch049
  FullyConstrained = true
  MapMode = 5
  Placement = pos=(0,0,0) rot=(1,0,0;1.5708rad)
  Support = -> [XZ_Plane066]
  sketch-geometry (2):
    g0: Circle CenterX=0 CenterY=0 CenterZ=0 NormalX=0 NormalY=0 NormalZ=1 AngleXU=0 Radius=6.35
    g1: Circle CenterX=0 CenterY=0 CenterZ=0 NormalX=0 NormalY=0 NormalZ=1 AngleXU=0 Radius=23.8125
  constraints (4):
    c: Coincident(g0,g-1)
    c: Coincident(g1,g0)
    c: Diameter(g1) = 47.625
    c: Diameter(g0) = 12.7
FEATURE [Sketcher::SketchObject] Sketch050
  FullyConstrained = true
  MapMode = 5
  Placement = pos=(0,0,0) rot=(1,0,0;1.5708rad)
  Support = -> [XZ_Plane064]
  sketch-geometry (1):
    g0: Circle CenterX=0 CenterY=0 CenterZ=0 NormalX=0 NormalY=0 NormalZ=1 AngleXU=0 Radius=14.2875
  constraints (2):
    c: Coincident(g0,g-1)
    c: Diameter(g0) = 28.575
FEATURE [PartDesign::Pad] Pad049
  Direction = (1,1,1)
  Length = 12.7
  Length2 = 100
  Placement = pos=(0,0,0) rot=(1,0,0;1.5708rad)
  Profile = -> Sketch050
  Type = 0
FEATURE [PartDesign::Body] Body048
  Group = -> [Sketch050,Pad049]
  Origin = -> Origin064
  Tip = -> Pad049
FEATURE [PartDesign::Pad] Pad050
  Direction = (1,1,1)
  Length = 25.4
  Length2 = 100
  Placement = pos=(0,0,0) rot=(1,0,0;1.5708rad)
  Profile = -> Sketch049
  Type = 0
FEATURE [PartDesign::Body] Body050
  Group = -> [Sketch049,Pad050]
  Origin = -> Origin066
  Tip = -> Pad050
FEATURE [Part::Cut] Cut047
  Base = -> Body050
  Tool = -> Body048
FEATURE [Part::Chamfer] Chamfer003
  Base = -> Cut047
  Edges = 1 edges: [Edge3 r1=4.76 r2=11.11]
  Placement = pos=(0,-12.7,0) rot=(0,0,1;0rad)
FEATURE [App::Part] Part013  label="CRDmount(simple)2"
  Group = -> [Body047,Body049,Cut041,Cut042,Cut043,Cut044,Cut045,Cut046,Chamfer005,Body050,Chamfer004,Body048,Cut047,Chamfer003]
  Origin = -> Origin065
  Placement = pos=(127,1096.44,139.05) rot=(0,0,1;3.14159rad)
FEATURE [Part::Feature] Solid060
  shape: bbox 16.51 x 30.48 x 30.48 mm, 270 faces (baked)
FEATURE [Part::Feature] Solid061
  shape: bbox 2.032 x 26.16 x 26.16 mm, 29 faces (baked)
FEATURE [Part::Compound2] Compound013  label="0370-E0W"
  Links = -> [Solid060,Solid061]
  Placement = pos=(0,22.1731,120) rot=(0,0,1;1.5708rad)
FEATURE [App::Part] Part011  label="Fiber"
  Group = -> [Solid039,Solid045,Solid040,Solid038,Solid042,Solid046,Solid041,Compound011,Solid043,Solid044,Compound010,Solid053,Solid052,Solid057,Solid058,Solid059,Solid055,Solid054,Solid056,Solid047,Solid048,Solid049,Solid050,Solid051,Compound012,Solid060,Solid061,Compound013]
  Origin = -> Origin056
  Placement = pos=(127,1185,19.05) rot=(0,0,1;3.14159rad)
FEATURE [Part::Feature] Solid063
  shape: bbox 4.001 x 12 x 4.001 mm, 40 faces (baked)
FEATURE [Part::Feature] Solid064
  shape: bbox 25 x 75 x 25 mm, 25 faces (baked)
FEATURE [Part::Feature] Solid065
  shape: bbox 3.482 x 3.482 x 3.175 mm, 21 faces (baked)
FEATURE [Part::Feature] Solid066
  shape: bbox 3.52 x 3.049 x 7.519 mm, 25 faces (baked)
FEATURE [Part::Feature] Solid067
  shape: bbox 12.67 x 75.01 x 12.67 mm, 32 faces (baked)
FEATURE [Part::Feature] Solid069
  shape: bbox 15.88 x 5.969 x 15.88 mm, 19 faces (baked)
FEATURE [Part::Feature] Solid070
  shape: bbox 14.48 x 14.48 x 16.13 mm, 310 faces (baked)
FEATURE [Part::Compound2] Compound016  label="0332-E0W004"
  Links = -> [Solid067,Solid063]
  Placement = pos=(0,0,22.45) rot=(1,0,0;1.5708rad)
FEATURE [Part::Feature] Solid071  label="19225-E0W004"
  Placement = pos=(0,0,5) rot=(1,0,0;1.5708rad)
  shape: bbox 75 x 24.99 x 10 mm, 221 faces (baked)
FEATURE [Part::Feature] Solid072
  shape: bbox 2.997 x 2.997 x 3.556 mm, 8 faces (baked)
FEATURE [Part::Compound2] Compound014  label="23133-E0W004"
  Links = -> [Solid064,Solid069,Solid070,Solid072,Solid066,Solid065]
  Placement = pos=(-1.27,-4.75,41.95) rot=(1,0,0;1.5708rad)
FEATURE [App::Part] Part014  label="LightSourceMount"
  Group = -> [Solid071,Solid065,Solid072,Solid064,Solid070,Solid066,Solid069,Compound014,Solid067,Solid063,Compound016]
  Origin = -> Origin067
  Placement = pos=(127,25.4,19.05) rot=(0,0,1;0rad)
FEATURE [Sketcher::SketchObject] Sketch051
  FullyConstrained = true
  MapMode = 5
  Placement = pos=(0,0,0) rot=(1,0,0;1.5708rad)
  Support = -> [XZ_Plane069]
  sketch-geometry (4):
    g0: LineSegment StartX=-1.725 StartY=0 StartZ=0 EndX=1.725 EndY=0 EndZ=0
    g1: LineSegment StartX=-5.175 StartY=-13.8372 StartZ=0 EndX=5.175 EndY=-13.8372 EndZ=0
    g2: LineSegment StartX=-5.175 StartY=-13.8372 StartZ=0 EndX=-1.725 EndY=0 EndZ=0
    g3: LineSegment StartX=1.725 StartY=0 StartZ=0 EndX=5.175 EndY=-13.8372 EndZ=0
  constraints (12):
    c: Horizontal(g0)
    c: Horizontal(g1)
    c: Coincident(g2,g1)
    c: Coincident(g2,g0)
    c: Coincident(g3,g0)
    c: Coincident(g3,g1)
    c: Angle(g1,g2) = 1.32645
    c: Angle(g3,g1) = 1.32645
    c: DistanceX(g0,g0) = 3.45
    c: DistanceX(g1,g1) = 10.35
    c: DistanceX(g-1,g0) = 1.725
    c: DistanceY(g-1,g0) = 0
FEATURE [PartDesign::Pad] Pad051
  Direction = (1,1,1)
  Length = 45
  Length2 = 100
  Placement = pos=(0,0,0) rot=(1,0,0;1.5708rad)
  Profile = -> Sketch051
  Type = 0
FEATURE [PartDesign::Body] Body051
  Group = -> [Sketch051,Pad051]
  Origin = -> Origin069
  Placement = pos=(0,0,-8.75) rot=(0,0,1;0rad)
  Tip = -> Pad051
FEATURE [Sketcher::SketchObject] Sketch052
  FullyConstrained = true
  MapMode = 5
  Placement = pos=(0,0,0) rot=(1,0,0;1.5708rad)
  Support = -> [XZ_Plane070]
  sketch-geometry (2):
    g0: Circle CenterX=0 CenterY=0 CenterZ=0 NormalX=0 NormalY=0 NormalZ=1 AngleXU=0 Radius=4.5
    g1: Circle CenterX=0 CenterY=0 CenterZ=0 NormalX=0 NormalY=0 NormalZ=1 AngleXU=0 Radius=22.5
  constraints (4):
    c: Coincident(g0,g-1)
    c: Coincident(g1,g0)
    c: Diameter(g0) = 9
    c: Diameter(g1) = 45
FEATURE [PartDesign::Pad] Pad052
  Direction = (1,1,1)
  Length = 43
  Length2 = 100
  Placement = pos=(0,0,0) rot=(1,0,0;1.5708rad)
  Profile = -> Sketch052
  Type = 0
FEATURE [PartDesign::Body] Body052
  Group = -> [Sketch052,Pad052]
  Origin = -> Origin070
  Tip = -> Pad052
FEATURE [Part::Cut] Cut048
  Base = -> Body052
  Placement = pos=(0,0,0) rot=(0,1,0;0.523599rad)
  Tool = -> Body051
FEATURE [Part::Cut] Cut049
  Base = -> Cut048
  Placement = pos=(0,0,0) rot=(0,1,0;1.0472rad)
  Tool = -> Body051
FEATURE [Part::Cut] Cut050
  Base = -> Cut049
  Placement = pos=(0,0,0) rot=(0,1,0;0.523599rad)
  Tool = -> Body051
FEATURE [Part::Cut] Cut051
  Base = -> Cut050
  Placement = pos=(0,0,0) rot=(0,1,0;1.0472rad)
  Tool = -> Body051
FEATURE [Part::Cut] Cut052
  Base = -> Cut051
  Placement = pos=(0,0,0) rot=(0,1,0;0.523599rad)
  Tool = -> Body051
FEATURE [Part::Cut] Cut053
  Base = -> Cut052
  Placement = pos=(0,0,0) rot=(0,1,0;1.0472rad)
  Tool = -> Body051
FEATURE [Part::Cut] Cut054
  Base = -> Cut053
  Placement = pos=(0,0,0) rot=(0,1,0;0.523599rad)
  Tool = -> Body051
FEATURE [Part::Cut] Cut055
  Base = -> Cut054
  Placement = pos=(0,0,0) rot=(0,1,0;0.523599rad)
  Tool = -> Body051
FEATURE [Sketcher::SketchObject] Sketch053
  FullyConstrained = true
  MapMode = 5
  Placement = pos=(0,0,0) rot=(1,0,0;1.5708rad)
  Support = -> [XZ_Plane071]
  sketch-geometry (4):
    g0: LineSegment StartX=-2.68172 StartY=0 StartZ=0 EndX=2.68172 EndY=0 EndZ=0
    g1: LineSegment StartX=2.68172 StartY=0 StartZ=0 EndX=5.175 EndY=-10 EndZ=0
    g2: LineSegment StartX=5.175 StartY=-10 StartZ=0 EndX=-5.175 EndY=-10 EndZ=0
    g3: LineSegment StartX=-5.175 StartY=-10 StartZ=0 EndX=-2.68172 EndY=0 EndZ=0
  constraints (12):
    c: Coincident(g1,g0)
    c: Coincident(g2,g1)
    c: Coincident(g3,g2)
    c: Coincident(g3,g0)
    c: Horizontal(g0)
    c: Horizontal(g2)
    c: Angle(g2,g3) = 1.32645
    c: Angle(g1,g2) = 1.32645
    c: DistanceX(g2,g2) = 10.35
    c: DistanceY(g-1,g0) = 0
    c: DistanceY(g3,g3) = 10
    c: DistanceX(g2,g-1) = 5.175
FEATURE [PartDesign::Pad] Pad053
  Direction = (1,1,1)
  Length = 45
  Length2 = 100
  Placement = pos=(0,0,0) rot=(1,0,0;1.5708rad)
  Profile = -> Sketch053
  Type = 0
FEATURE [PartDesign::Body] Body053
  Group = -> [Sketch053,Pad053]
  Origin = -> Origin071
  Placement = pos=(0,0,-12.58) rot=(0,0,1;0rad)
  Tip = -> Pad053
FEATURE [Part::Cut] Cut056
  Base = -> Cut055
  Placement = pos=(0,0,0) rot=(0,1,0;1.5708rad)
  Tool = -> Body053
FEATURE [Part::Cut] Cut057
  Base = -> Cut056
  Placement = pos=(0,0,0) rot=(0,1,0;1.5708rad)
  Tool = -> Body053
FEATURE [Part::Cut] Cut058
  Base = -> Cut057
  Placement = pos=(0,0,0) rot=(0,1,0;1.5708rad)
  Tool = -> Body053
FEATURE [Part::Cut] Cut059
  Base = -> Cut058
  Placement = pos=(0,-7,0) rot=(0,0,1;0rad)
  Tool = -> Body053
FEATURE [Sketcher::SketchObject] Sketch054
  FullyConstrained = true
  MapMode = 5
  Placement = pos=(0,0,0) rot=(1,0,0;1.5708rad)
  Support = -> [XZ_Plane072]
  sketch-geometry (2):
    g0: Circle CenterX=0 CenterY=0 CenterZ=0 NormalX=0 NormalY=0 NormalZ=1 AngleXU=0 Radius=22.5
    g1: Circle CenterX=0 CenterY=0 CenterZ=0 NormalX=0 NormalY=0 NormalZ=1 AngleXU=0 Radius=4.5
  constraints (4):
    c: Coincident(g0,g-1)
    c: Coincident(g1,g0)
    c: Diameter(g1) = 9
    c: Diameter(g0) = 45
FEATURE [PartDesign::Pad] Pad054
  Direction = (1,1,1)
  Length = 7
  Length2 = 100
  Placement = pos=(0,0,0) rot=(1,0,0;1.5708rad)
  Profile = -> Sketch054
  Type = 0
FEATURE [PartDesign::Body] Body054
  Group = -> [Sketch054,Pad054]
  Origin = -> Origin072
  Tip = -> Pad054
FEATURE [Part::MultiFuse] Fusion003  label="HeatSink"
  Placement = pos=(0,3.5,0) rot=(0,0,1;0rad)
  Shapes = -> [Cut059,Body054]
FEATURE [Part::Feature] Solid073  label="CTN011214"
  shape: bbox 18.16 x 4.9 x 168.1 mm, 299 faces (baked)
FEATURE [Sketcher::SketchObject] Sketch055
  FullyConstrained = true
  MapMode = 5
  Placement = pos=(0,0,0) rot=(1,0,0;1.5708rad)
  Support = -> [XZ_Plane073]
  sketch-geometry (4):
    g0: LineSegment StartX=-25.5 StartY=163.29 StartZ=0 EndX=20.73 EndY=163.29 EndZ=0
    g1: LineSegment StartX=20.73 StartY=163.29 StartZ=0 EndX=20.73 EndY=27.91 EndZ=0
    g2: LineSegment StartX=20.73 StartY=27.91 StartZ=0 EndX=-25.5 EndY=27.91 EndZ=0
    g3: LineSegment StartX=-25.5 StartY=27.91 StartZ=0 EndX=-25.5 EndY=163.29 EndZ=0
  constraints (12):
    c: Coincident(g0,g1)
    c: Coincident(g1,g2)
    c: Coincident(g2,g3)
    c: Coincident(g3,g0)
    c: Horizontal(g0)
    c: Horizontal(g2)
    c: Vertical(g1)
    c: Vertical(g3)
    c: DistanceY(g1,g1) = 135.38
    c: DistanceX(g2,g2) = 46.23
    c: DistanceY(g-1,g1) = 27.91
    c: DistanceX(g-1,g1) = 20.73
FEATURE [PartDesign::Pad] Pad055
  Direction = (1,1,1)
  Length = 10
  Length2 = 100
  Placement = pos=(0,0,0) rot=(1,0,0;1.5708rad)
  Profile = -> Sketch055
  Type = 0
FEATURE [PartDesign::Body] Body055
  Group = -> [Sketch055,Pad055]
  Origin = -> Origin073
  Placement = pos=(0,5,0) rot=(0,0,1;0rad)
  Tip = -> Pad055
FEATURE [Part::Cut] Cut060  label="TEC"
  Base = -> Solid073
  Placement = pos=(0,5.95,0) rot=(0,0,1;0rad)
  Tool = -> Body055
FEATURE [Sketcher::SketchObject] Sketch056
  FullyConstrained = true
  MapMode = 5
  Placement = pos=(0,0,0) rot=(1,0,0;1.5708rad)
  Support = -> [XZ_Plane074]
  sketch-geometry (1):
    g0: Circle CenterX=0 CenterY=0 CenterZ=0 NormalX=0 NormalY=0 NormalZ=1 AngleXU=0 Radius=22.5
  constraints (2):
    c: Coincident(g0,g-1)
    c: Diameter(g0) = 45
FEATURE [PartDesign::Pad] Pad056
  Direction = (1,1,1)
  Length = 6.35
  Length2 = 100
  Placement = pos=(0,0,0) rot=(1,0,0;1.5708rad)
  Profile = -> Sketch056
  Type = 0
FEATURE [PartDesign::Body] Body056
  Group = -> [Sketch056,Pad056]
  Origin = -> Origin074
  Tip = -> Pad056
FEATURE [Sketcher::SketchObject] Sketch057
  FullyConstrained = true
  MapMode = 5
  Placement = pos=(0,0,0) rot=(1,0,0;1.5708rad)
  Support = -> [XZ_Plane075]
  sketch-geometry (1):
    g0: Circle CenterX=0 CenterY=0 CenterZ=0 NormalX=0 NormalY=0 NormalZ=1 AngleXU=0 Radius=2.5
  constraints (2):
    c: Coincident(g0,g-1)
    c: Diameter(g0) = 5
FEATURE [PartDesign::Pad] Pad057
  Direction = (1,1,1)
  Length = 4
  Length2 = 100
  Placement = pos=(0,0,0) rot=(1,0,0;1.5708rad)
  Profile = -> Sketch057
  Type = 0
FEATURE [PartDesign::Body] Body057
  Group = -> [Sketch057,Pad057]
  Origin = -> Origin075
  Placement = pos=(10,0,-10) rot=(0,0,1;0rad)
  Tip = -> Pad057
FEATURE [Part::Cut] Cut061
  Base = -> Body056
  Tool = -> Body057
FEATURE [Sketcher::SketchObject] Sketch058
  FullyConstrained = true
  MapMode = 5
  Placement = pos=(0,0,0) rot=(1,0,0;1.5708rad)
  sketch-geometry (4):
    g0: LineSegment StartX=0 StartY=0 StartZ=0 EndX=10 EndY=0 EndZ=0
    g1: LineSegment StartX=10 StartY=0 StartZ=0 EndX=10 EndY=-3 EndZ=0
    g2: LineSegment StartX=10 StartY=-3 StartZ=0 EndX=0 EndY=-3 EndZ=0
    g3: LineSegment StartX=0 StartY=-3 StartZ=0 EndX=0 EndY=0 EndZ=0
  constraints (11):
    c: Coincident(g0,g1)
    c: Coincident(g1,g2)
    c: Coincident(g2,g3)
    c: Coincident(g3,g0)
    c: Horizontal(g0)
    c: Horizontal(g2)
    c: Vertical(g1)
    c: Vertical(g3)
    c: Coincident(g0,g-1)
    c: DistanceX(g2,g2) = 10
    c: DistanceY(g1,g1) = 3
FEATURE [PartDesign::Pad] Pad058
  Direction = (1,1,1)
  Length = 3
  Length2 = 100
  Placement = pos=(0,0,0) rot=(1,0,0;1.5708rad)
  Profile = -> Sketch058
  Type = 0
FEATURE [Part::Fillet] Fillet
  Base = -> Pad058
  Edges = 1 edges r=0.5: [Edge5]
FEATURE [Part::Fillet] Fillet001
  Base = -> Fillet
  Edges = 1 edges r=0.5: [Edge2]
  Placement = pos=(-23,0,0) rot=(0,0,1;0rad)
FEATURE [Part::Cut] Cut062  label="LEDplate"
  Base = -> Cut061
  Placement = pos=(0,14.75,0) rot=(0,0,1;0rad)
  Tool = -> Fillet001
FEATURE [Part::Sphere] Sphere
  Angle1 = -90
  Angle2 = 90
  Angle3 = 360
  AttacherType = Attacher::AttachEngine3D
  Radius = 1.6
FEATURE [Sketcher::SketchObject] Sketch059
  FullyConstrained = true
  MapMode = 5
  Placement = pos=(0,0,0) rot=(1,0,0;1.5708rad)
  Support = -> [XZ_Plane076]
  sketch-geometry (4):
    g0: LineSegment StartX=0 StartY=0 StartZ=0 EndX=5 EndY=0 EndZ=0
    g1: LineSegment StartX=5 StartY=0 StartZ=0 EndX=5 EndY=-5 EndZ=0
    g2: LineSegment StartX=5 StartY=-5 StartZ=0 EndX=0 EndY=-5 EndZ=0
    g3: LineSegment StartX=0 StartY=-5 StartZ=0 EndX=0 EndY=0 EndZ=0
  constraints (11):
    c: Coincident(g0,g1)
    c: Coincident(g1,g2)
    c: Coincident(g2,g3)
    c: Coincident(g3,g0)
    c: Horizontal(g0)
    c: Horizontal(g2)
    c: Vertical(g1)
    c: Vertical(g3)
    c: Coincident(g0,g-1)
    c: DistanceX(g0,g0) = 5
    c: DistanceY(g1,g1) = 5
FEATURE [PartDesign::Pad] Pad059
  Direction = (1,1,1)
  Length = 5
  Length2 = 100
  Placement = pos=(0,0,0) rot=(1,0,0;1.5708rad)
  Profile = -> Sketch059
  Type = 0
FEATURE [PartDesign::Body] Body058
  Group = -> [Sketch059,Pad059]
  Origin = -> Origin076
  Placement = pos=(-2,0,2) rot=(0,0,1;0rad)
  Tip = -> Pad059
FEATURE [Part::Cut] Cut063
  Base = -> Sphere
  Tool = -> Body058
FEATURE [Sketcher::SketchObject] Sketch060
  FullyConstrained = true
  MapMode = 5
  Placement = pos=(0,0,0) rot=(1,0,0;1.5708rad)
  Support = -> [XZ_Plane077]
  sketch-geometry (4):
    g0: LineSegment StartX=0 StartY=0 StartZ=0 EndX=4.4 EndY=0 EndZ=0
    g1: LineSegment StartX=4.4 StartY=0 StartZ=0 EndX=4.4 EndY=-4.4 EndZ=0
    g2: LineSegment StartX=4.4 StartY=-4.4 StartZ=0 EndX=0 EndY=-4.4 EndZ=0
    g3: LineSegment StartX=0 StartY=-4.4 StartZ=0 EndX=0 EndY=0 EndZ=0
  constraints (11):
    c: Coincident(g0,g1)
    c: Coincident(g1,g2)
    c: Coincident(g2,g3)
    c: Coincident(g3,g0)
    c: Horizontal(g0)
    c: Horizontal(g2)
    c: Vertical(g1)
    c: Vertical(g3)
    c: Coincident(g0,g-1)
    c: DistanceX(g0,g0) = 4.4
    c: DistanceY(g1,g1) = 4.4
FEATURE [PartDesign::Pad] Pad060
  Direction = (1,1,1)
  Length = 0.5
  Length2 = 100
  Placement = pos=(0,0,0) rot=(1,0,0;1.5708rad)
  Profile = -> Sketch060
  Type = 0
FEATURE [PartDesign::Body] Body059
  Group = -> [Sketch060,Pad060]
  Origin = -> Origin077
  Placement = pos=(-2.2,0,2.2) rot=(0,0,1;0rad)
  Tip = -> Pad060
FEATURE [Sketcher::SketchObject] Sketch061
  FullyConstrained = true
  MapMode = 5
  Placement = pos=(0,0,0) rot=(1,0,0;1.5708rad)
  Support = -> [XZ_Plane078]
  sketch-geometry (1):
    g0: Circle CenterX=0 CenterY=0 CenterZ=0 NormalX=0 NormalY=0 NormalZ=1 AngleXU=0 Radius=9.95
  constraints (2):
    c: Coincident(g0,g-1)
    c: Diameter(g0) = 19.9
FEATURE [PartDesign::Pad] Pad061
  Direction = (1,1,1)
  Length = 1.75
  Length2 = 100
  Placement = pos=(0,0,0) rot=(1,0,0;1.5708rad)
  Profile = -> Sketch061
  Type = 0
FEATURE [PartDesign::Body] Body060
  Group = -> [Sketch061,Pad061]
  Origin = -> Origin078
  Placement = pos=(0,-0.5,0) rot=(0,0,1;0rad)
  Tip = -> Pad061
FEATURE [Part::MultiFuse] Fusion004  label="LEDsimple"
  Placement = pos=(0,17,0) rot=(0,0,1;0rad)
  Shapes = -> [Cut063,Body059,Body060]
FEATURE [App::Part] Part015  label="LightSource"
  Group = -> [Cut055,Cut050,Cut049,Body052,Body051,Cut048,Cut058,Cut052,Cut054,Cut053,Cut051,Body053,Cut057,Body054,Cut056,Cut059,Fusion003,Solid073,Body055,Cut060,Body056,Body057,Cut061,Pad058,Sketch058,Fillet,Fillet001,Cut062,Cut063,Body058,Sphere,Body059,Body060,Fusion004]
  Origin = -> Origin068
  Placement = pos=(127,25.4,139.05) rot=(0,0,1;0rad)
